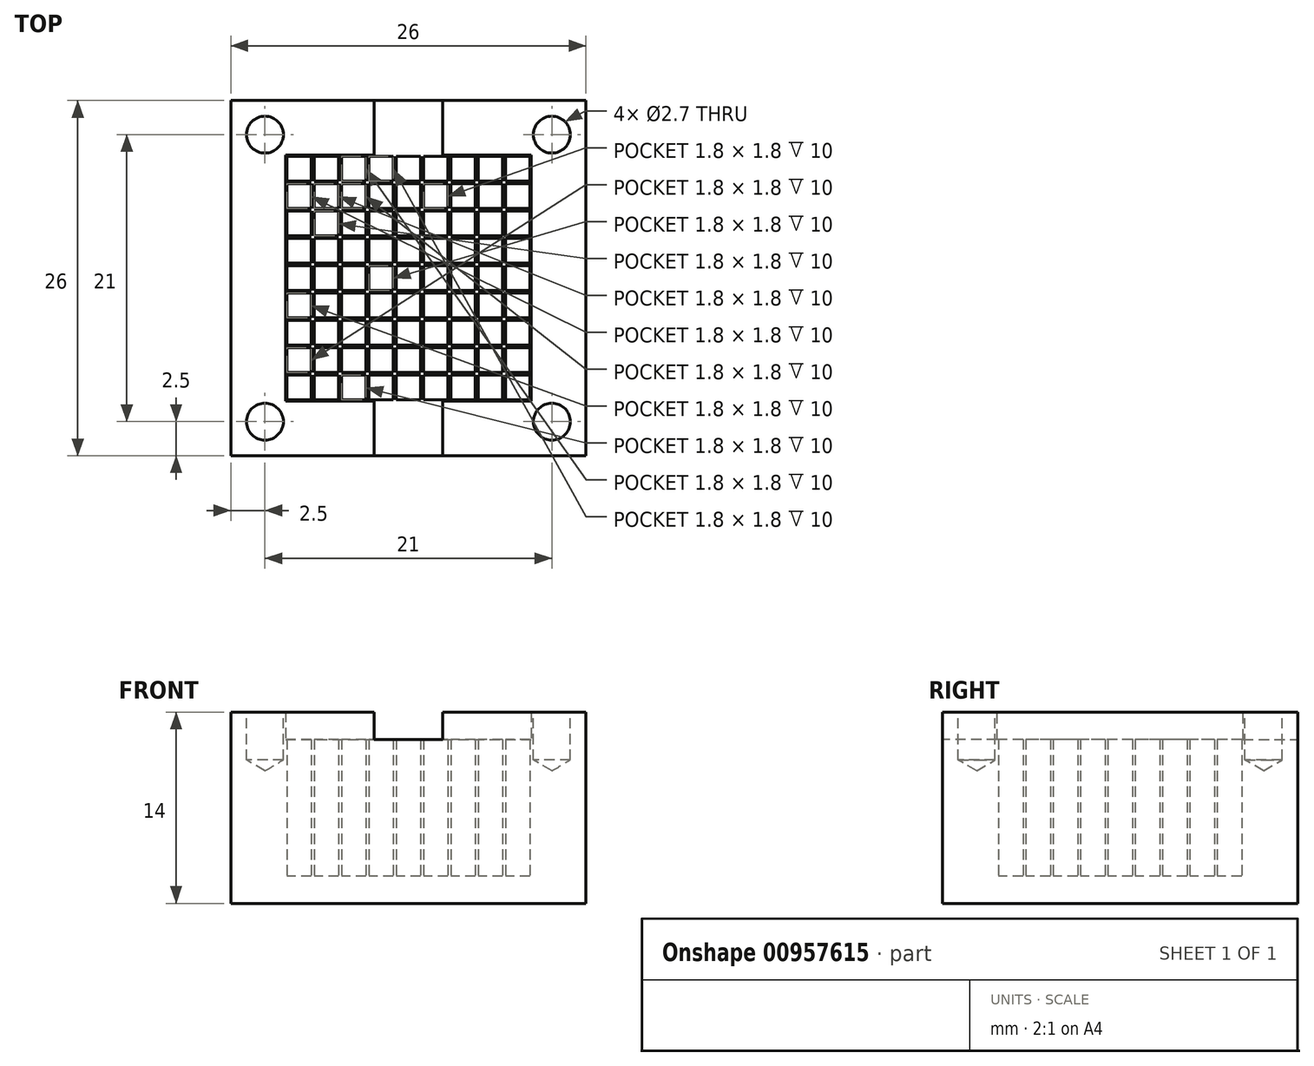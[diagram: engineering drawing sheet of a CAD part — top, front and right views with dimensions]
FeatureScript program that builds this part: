
annotation { "Feature Type Name" : "Feature", "Feature Type Description" : "" }
export const myFeature = defineFeature(function(context is Context, id is Id, definition is map)
    precondition{}
    {
        {
            var Q0;
            Q0=qCreatedBy(makeId("Top.planeOp"),FACE);
            var sketch = newSketch(context, id + "F0", { "sketchPlane" : qUnion([Q0])});
            skLineSegment(sketch, "E0.bottom", {"start": v(-9, 9) * mm, "end": v(9, 9) * mm});
            skLineSegment(sketch, "E0.top", {"start": v(-9, -9) * mm, "end": v(9, -9) * mm});
            skLineSegment(sketch, "E0.left", {"start": v(-9, 9) * mm, "end": v(-9, -9) * mm});
            skLineSegment(sketch, "E0.right", {"start": v(9, 9) * mm, "end": v(9, -9) * mm});
            skPoint(sketch, "E0.middle", {"position": v(0, 0) * mm});
            skLineSegment(sketch, "E1", {"start": v(-8.9, 9) * mm, "end": v(-8.9, -9) * mm});
            skLineSegment(sketch, "E2", {"start": v(-7.1, 9) * mm, "end": v(-7.1, -9) * mm});
            skLineSegment(sketch, "E3", {"start": v(-6.9, 9) * mm, "end": v(-6.9, -9) * mm});
            skLineSegment(sketch, "E4", {"start": v(-5.1, 9) * mm, "end": v(-5.1, -9) * mm});
            skLineSegment(sketch, "E5", {"start": v(-4.9, 9) * mm, "end": v(-4.9, -9) * mm});
            skLineSegment(sketch, "E6", {"start": v(-3.1, 9) * mm, "end": v(-3.1, -9) * mm});
            skLineSegment(sketch, "E7", {"start": v(-2.9, 9) * mm, "end": v(-2.9, -9) * mm});
            skLineSegment(sketch, "E8", {"start": v(-1.1, 9) * mm, "end": v(-1.1, -9) * mm});
            skLineSegment(sketch, "E9", {"start": v(-0.9, 9) * mm, "end": v(-0.9, -9) * mm});
            skLineSegment(sketch, "E10", {"start": v(0.9, 9) * mm, "end": v(0.9, -9) * mm});
            skLineSegment(sketch, "E11", {"start": v(1.1, 9) * mm, "end": v(1.1, -9) * mm});
            skLineSegment(sketch, "E12", {"start": v(2.9, 9) * mm, "end": v(2.9, -9) * mm});
            skLineSegment(sketch, "E13", {"start": v(3.1, 9) * mm, "end": v(3.1, -9) * mm});
            skLineSegment(sketch, "E14", {"start": v(4.9, 9) * mm, "end": v(4.9, -9) * mm});
            skLineSegment(sketch, "E15", {"start": v(5.1, 9) * mm, "end": v(5.1, -9) * mm});
            skLineSegment(sketch, "E16", {"start": v(6.9, 9) * mm, "end": v(6.9, -9) * mm});
            skLineSegment(sketch, "E17", {"start": v(7.1, 9) * mm, "end": v(7.1, -9) * mm});
            skLineSegment(sketch, "E18", {"start": v(8.9, 9) * mm, "end": v(8.9, -9) * mm});
            skLineSegment(sketch, "E19", {"start": v(9, 8.9) * mm, "end": v(-9, 8.9) * mm});
            skLineSegment(sketch, "E20", {"start": v(9, 7.1) * mm, "end": v(-9, 7.1) * mm});
            skLineSegment(sketch, "E21", {"start": v(9, 6.9) * mm, "end": v(-9, 6.9) * mm});
            skLineSegment(sketch, "E22", {"start": v(9, 5.1) * mm, "end": v(-9, 5.1) * mm});
            skLineSegment(sketch, "E23", {"start": v(9, 4.9) * mm, "end": v(-9, 4.9) * mm});
            skLineSegment(sketch, "E24", {"start": v(9, 3.1) * mm, "end": v(-9, 3.1) * mm});
            skLineSegment(sketch, "E25", {"start": v(9, 2.9) * mm, "end": v(-9, 2.9) * mm});
            skLineSegment(sketch, "E26", {"start": v(9, 1.1) * mm, "end": v(-9, 1.1) * mm});
            skLineSegment(sketch, "E27", {"start": v(9, 0.9) * mm, "end": v(-9, 0.9) * mm});
            skLineSegment(sketch, "E28", {"start": v(9, -0.9) * mm, "end": v(-9, -0.9) * mm});
            skLineSegment(sketch, "E29", {"start": v(9, -1.1) * mm, "end": v(-9, -1.1) * mm});
            skLineSegment(sketch, "E30", {"start": v(9, -2.9) * mm, "end": v(-9, -2.9) * mm});
            skLineSegment(sketch, "E31", {"start": v(9, -3.1) * mm, "end": v(-9, -3.1) * mm});
            skLineSegment(sketch, "E32", {"start": v(9, -4.9) * mm, "end": v(-9, -4.9) * mm});
            skLineSegment(sketch, "E33", {"start": v(9, -5.1) * mm, "end": v(-9, -5.1) * mm});
            skLineSegment(sketch, "E34", {"start": v(9, -6.9) * mm, "end": v(-9, -6.9) * mm});
            skLineSegment(sketch, "E35", {"start": v(9, -7.1) * mm, "end": v(-9, -7.1) * mm});
            skLineSegment(sketch, "E36", {"start": v(9, -8.9) * mm, "end": v(-9, -8.9) * mm});
            skSolve(sketch);
        }
        {
            var Q0;
            {var subQ0=sQuery(id+"F0.wireOp",EDGE,"E30");var subQ1=sQuery(id+"F0.wireOp",EDGE,"E10");var subQ2=makeQuery(id+"F0.imprint","INTERSECT",VERTEX,{"derivedFrom":[subQ1,subQ0]});Q0=makeQuery(id+"F0.imprint","IMPRINT",FACE,{"disambiguationData":[TD([[makeQuery(id+"F0.imprint","IMPRINT",EDGE,{"disambiguationData":[TD([[subQ2,-1.0]])],"derivedFrom":subQ1}),1.0]])]});}
            var Q1;
            {var subQ0=sQuery(id+"F0.wireOp",EDGE,"E26");var subQ1=sQuery(id+"F0.wireOp",EDGE,"E11");var subQ2=makeQuery(id+"F0.imprint","INTERSECT",VERTEX,{"derivedFrom":[subQ1,subQ0]});Q1=makeQuery(id+"F0.imprint","IMPRINT",FACE,{"disambiguationData":[TD([[makeQuery(id+"F0.imprint","IMPRINT",EDGE,{"disambiguationData":[TD([[subQ2,-1.0]])],"derivedFrom":subQ1}),1.0]])]});}
            var Q2;
            {var subQ0=sQuery(id+"F0.wireOp",EDGE,"E25");var subQ1=sQuery(id+"F0.wireOp",EDGE,"E8");var subQ2=makeQuery(id+"F0.imprint","INTERSECT",VERTEX,{"derivedFrom":[subQ1,subQ0]});Q2=makeQuery(id+"F0.imprint","IMPRINT",FACE,{"disambiguationData":[TD([[makeQuery(id+"F0.imprint","IMPRINT",EDGE,{"disambiguationData":[TD([[subQ2,-1.0]])],"derivedFrom":subQ1}),1.0]])]});}
            var Q3;
            {var subQ0=sQuery(id+"F0.wireOp",EDGE,"E24");var subQ1=sQuery(id+"F0.wireOp",EDGE,"E10");var subQ2=makeQuery(id+"F0.imprint","INTERSECT",VERTEX,{"derivedFrom":[subQ1,subQ0]});Q3=makeQuery(id+"F0.imprint","IMPRINT",FACE,{"disambiguationData":[TD([[makeQuery(id+"F0.imprint","IMPRINT",EDGE,{"disambiguationData":[TD([[subQ2,-1.0]])],"derivedFrom":subQ1}),1.0]])]});}
            var Q4;
            {var subQ0=sQuery(id+"F0.wireOp",EDGE,"E30");var subQ1=sQuery(id+"F0.wireOp",EDGE,"E15");var subQ2=makeQuery(id+"F0.imprint","INTERSECT",VERTEX,{"derivedFrom":[subQ1,subQ0]});Q4=makeQuery(id+"F0.imprint","IMPRINT",FACE,{"disambiguationData":[TD([[makeQuery(id+"F0.imprint","IMPRINT",EDGE,{"disambiguationData":[TD([[subQ2,-1.0]])],"derivedFrom":subQ1}),1.0]])]});}
            var Q5;
            {var subQ0=sQuery(id+"F0.wireOp",EDGE,"E35");var subQ1=sQuery(id+"F0.wireOp",EDGE,"E12");var subQ2=makeQuery(id+"F0.imprint","INTERSECT",VERTEX,{"derivedFrom":[subQ1,subQ0]});Q5=makeQuery(id+"F0.imprint","IMPRINT",FACE,{"disambiguationData":[TD([[makeQuery(id+"F0.imprint","IMPRINT",EDGE,{"disambiguationData":[TD([[subQ2,-1.0]])],"derivedFrom":subQ1}),1.0]])]});}
            var Q6;
            {var subQ0=sQuery(id+"F0.wireOp",EDGE,"E35");var subQ1=sQuery(id+"F0.wireOp",EDGE,"E14");var subQ2=makeQuery(id+"F0.imprint","INTERSECT",VERTEX,{"derivedFrom":[subQ1,subQ0]});Q6=makeQuery(id+"F0.imprint","IMPRINT",FACE,{"disambiguationData":[TD([[makeQuery(id+"F0.imprint","IMPRINT",EDGE,{"disambiguationData":[TD([[subQ2,-1.0]])],"derivedFrom":subQ1}),1.0]])]});}
            var Q7;
            {var subQ0=sQuery(id+"F0.wireOp",EDGE,"E32");var subQ1=sQuery(id+"F0.wireOp",EDGE,"E10");var subQ2=makeQuery(id+"F0.imprint","INTERSECT",VERTEX,{"derivedFrom":[subQ1,subQ0]});Q7=makeQuery(id+"F0.imprint","IMPRINT",FACE,{"disambiguationData":[TD([[makeQuery(id+"F0.imprint","IMPRINT",EDGE,{"disambiguationData":[TD([[subQ2,-1.0]])],"derivedFrom":subQ1}),1.0]])]});}
            var Q8;
            {var subQ0=sQuery(id+"F0.wireOp",EDGE,"E23");var subQ1=sQuery(id+"F0.wireOp",EDGE,"E14");var subQ2=makeQuery(id+"F0.imprint","INTERSECT",VERTEX,{"derivedFrom":[subQ1,subQ0]});Q8=makeQuery(id+"F0.imprint","IMPRINT",FACE,{"disambiguationData":[TD([[makeQuery(id+"F0.imprint","IMPRINT",EDGE,{"disambiguationData":[TD([[subQ2,-1.0]])],"derivedFrom":subQ1}),1.0]])]});}
            var Q9;
            {var subQ0=sQuery(id+"F0.wireOp",EDGE,"E23");var subQ1=sQuery(id+"F0.wireOp",EDGE,"E16");var subQ2=makeQuery(id+"F0.imprint","INTERSECT",VERTEX,{"derivedFrom":[subQ1,subQ0]});Q9=makeQuery(id+"F0.imprint","IMPRINT",FACE,{"disambiguationData":[TD([[makeQuery(id+"F0.imprint","IMPRINT",EDGE,{"disambiguationData":[TD([[subQ2,-1.0]])],"derivedFrom":subQ1}),1.0]])]});}
            var Q10;
            {var subQ0=sQuery(id+"F0.wireOp",EDGE,"E22");var subQ1=sQuery(id+"F0.wireOp",EDGE,"E9");var subQ2=makeQuery(id+"F0.imprint","INTERSECT",VERTEX,{"derivedFrom":[subQ1,subQ0]});Q10=makeQuery(id+"F0.imprint","IMPRINT",FACE,{"disambiguationData":[TD([[makeQuery(id+"F0.imprint","IMPRINT",EDGE,{"disambiguationData":[TD([[subQ2,-1.0]])],"derivedFrom":subQ1}),1.0]])]});}
            var Q11;
            {var subQ0=sQuery(id+"F0.wireOp",EDGE,"E27");var subQ1=sQuery(id+"F0.wireOp",EDGE,"E10");var subQ2=makeQuery(id+"F0.imprint","INTERSECT",VERTEX,{"derivedFrom":[subQ1,subQ0]});Q11=makeQuery(id+"F0.imprint","IMPRINT",FACE,{"disambiguationData":[TD([[makeQuery(id+"F0.imprint","IMPRINT",EDGE,{"disambiguationData":[TD([[subQ2,-1.0]])],"derivedFrom":subQ1}),1.0]])]});}
            var Q12;
            {var subQ0=sQuery(id+"F0.wireOp",EDGE,"E31");var subQ1=sQuery(id+"F0.wireOp",EDGE,"E2");var subQ2=makeQuery(id+"F0.imprint","INTERSECT",VERTEX,{"derivedFrom":[subQ1,subQ0]});Q12=makeQuery(id+"F0.imprint","IMPRINT",FACE,{"disambiguationData":[TD([[makeQuery(id+"F0.imprint","IMPRINT",EDGE,{"disambiguationData":[TD([[subQ2,-1.0]])],"derivedFrom":subQ1}),1.0]])]});}
            var Q13;
            {var subQ0=sQuery(id+"F0.wireOp",EDGE,"E30");var subQ1=sQuery(id+"F0.wireOp",EDGE,"E13");var subQ2=makeQuery(id+"F0.imprint","INTERSECT",VERTEX,{"derivedFrom":[subQ1,subQ0]});Q13=makeQuery(id+"F0.imprint","IMPRINT",FACE,{"disambiguationData":[TD([[makeQuery(id+"F0.imprint","IMPRINT",EDGE,{"disambiguationData":[TD([[subQ2,-1.0]])],"derivedFrom":subQ1}),1.0]])]});}
            var Q14;
            {var subQ0=sQuery(id+"F0.wireOp",EDGE,"E33");var subQ1=sQuery(id+"F0.wireOp",EDGE,"E16");var subQ2=makeQuery(id+"F0.imprint","INTERSECT",VERTEX,{"derivedFrom":[subQ1,subQ0]});Q14=makeQuery(id+"F0.imprint","IMPRINT",FACE,{"disambiguationData":[TD([[makeQuery(id+"F0.imprint","IMPRINT",EDGE,{"disambiguationData":[TD([[subQ2,-1.0]])],"derivedFrom":subQ1}),1.0]])]});}
            var Q15;
            {var subQ0=sQuery(id+"F0.wireOp",EDGE,"E29");var subQ1=sQuery(id+"F0.wireOp",EDGE,"E8");var subQ2=makeQuery(id+"F0.imprint","INTERSECT",VERTEX,{"derivedFrom":[subQ1,subQ0]});Q15=makeQuery(id+"F0.imprint","IMPRINT",FACE,{"disambiguationData":[TD([[makeQuery(id+"F0.imprint","IMPRINT",EDGE,{"disambiguationData":[TD([[subQ2,-1.0]])],"derivedFrom":subQ1}),1.0]])]});}
            var Q16;
            {var subQ0=sQuery(id+"F0.wireOp",EDGE,"E26");var subQ1=sQuery(id+"F0.wireOp",EDGE,"E1");var subQ2=makeQuery(id+"F0.imprint","INTERSECT",VERTEX,{"derivedFrom":[subQ1,subQ0]});Q16=makeQuery(id+"F0.imprint","IMPRINT",FACE,{"disambiguationData":[TD([[makeQuery(id+"F0.imprint","IMPRINT",EDGE,{"disambiguationData":[TD([[subQ2,-1.0]])],"derivedFrom":subQ1}),1.0]])]});}
            var Q17;
            {var subQ0=sQuery(id+"F0.wireOp",EDGE,"E30");var subQ1=sQuery(id+"F0.wireOp",EDGE,"E12");var subQ2=makeQuery(id+"F0.imprint","INTERSECT",VERTEX,{"derivedFrom":[subQ1,subQ0]});Q17=makeQuery(id+"F0.imprint","IMPRINT",FACE,{"disambiguationData":[TD([[makeQuery(id+"F0.imprint","IMPRINT",EDGE,{"disambiguationData":[TD([[subQ2,-1.0]])],"derivedFrom":subQ1}),1.0]])]});}
            var Q18;
            {var subQ0=sQuery(id+"F0.wireOp",EDGE,"E29");var subQ1=sQuery(id+"F0.wireOp",EDGE,"E12");var subQ2=makeQuery(id+"F0.imprint","INTERSECT",VERTEX,{"derivedFrom":[subQ1,subQ0]});Q18=makeQuery(id+"F0.imprint","IMPRINT",FACE,{"disambiguationData":[TD([[makeQuery(id+"F0.imprint","IMPRINT",EDGE,{"disambiguationData":[TD([[subQ2,-1.0]])],"derivedFrom":subQ1}),1.0]])]});}
            var Q19;
            {var subQ0=sQuery(id+"F0.wireOp",EDGE,"E31");var subQ1=sQuery(id+"F0.wireOp",EDGE,"E6");var subQ2=makeQuery(id+"F0.imprint","INTERSECT",VERTEX,{"derivedFrom":[subQ1,subQ0]});Q19=makeQuery(id+"F0.imprint","IMPRINT",FACE,{"disambiguationData":[TD([[makeQuery(id+"F0.imprint","IMPRINT",EDGE,{"disambiguationData":[TD([[subQ2,-1.0]])],"derivedFrom":subQ1}),1.0]])]});}
            var Q20;
            {var subQ0=sQuery(id+"F0.wireOp",EDGE,"E29");var subQ1=sQuery(id+"F0.wireOp",EDGE,"E10");var subQ2=makeQuery(id+"F0.imprint","INTERSECT",VERTEX,{"derivedFrom":[subQ1,subQ0]});Q20=makeQuery(id+"F0.imprint","IMPRINT",FACE,{"disambiguationData":[TD([[makeQuery(id+"F0.imprint","IMPRINT",EDGE,{"disambiguationData":[TD([[subQ2,-1.0]])],"derivedFrom":subQ1}),1.0]])]});}
            var Q21;
            {var subQ0=sQuery(id+"F0.wireOp",EDGE,"E25");var subQ1=sQuery(id+"F0.wireOp",EDGE,"E16");var subQ2=makeQuery(id+"F0.imprint","INTERSECT",VERTEX,{"derivedFrom":[subQ1,subQ0]});Q21=makeQuery(id+"F0.imprint","IMPRINT",FACE,{"disambiguationData":[TD([[makeQuery(id+"F0.imprint","IMPRINT",EDGE,{"disambiguationData":[TD([[subQ2,-1.0]])],"derivedFrom":subQ1}),1.0]])]});}
            var Q22;
            {var subQ0=sQuery(id+"F0.wireOp",EDGE,"E35");var subQ1=sQuery(id+"F0.wireOp",EDGE,"E16");var subQ2=makeQuery(id+"F0.imprint","INTERSECT",VERTEX,{"derivedFrom":[subQ1,subQ0]});Q22=makeQuery(id+"F0.imprint","IMPRINT",FACE,{"disambiguationData":[TD([[makeQuery(id+"F0.imprint","IMPRINT",EDGE,{"disambiguationData":[TD([[subQ2,-1.0]])],"derivedFrom":subQ1}),1.0]])]});}
            var Q23;
            {var subQ0=sQuery(id+"F0.wireOp",EDGE,"E31");var subQ1=sQuery(id+"F0.wireOp",EDGE,"E12");var subQ2=makeQuery(id+"F0.imprint","INTERSECT",VERTEX,{"derivedFrom":[subQ1,subQ0]});Q23=makeQuery(id+"F0.imprint","IMPRINT",FACE,{"disambiguationData":[TD([[makeQuery(id+"F0.imprint","IMPRINT",EDGE,{"disambiguationData":[TD([[subQ2,-1.0]])],"derivedFrom":subQ1}),1.0]])]});}
            var Q24;
            {var subQ0=sQuery(id+"F0.wireOp",EDGE,"E24");var subQ1=sQuery(id+"F0.wireOp",EDGE,"E1");var subQ2=makeQuery(id+"F0.imprint","INTERSECT",VERTEX,{"derivedFrom":[subQ1,subQ0]});Q24=makeQuery(id+"F0.imprint","IMPRINT",FACE,{"disambiguationData":[TD([[makeQuery(id+"F0.imprint","IMPRINT",EDGE,{"disambiguationData":[TD([[subQ2,-1.0]])],"derivedFrom":subQ1}),1.0]])]});}
            var Q25;
            {var subQ0=sQuery(id+"F0.wireOp",EDGE,"E27");var subQ1=sQuery(id+"F0.wireOp",EDGE,"E16");var subQ2=makeQuery(id+"F0.imprint","INTERSECT",VERTEX,{"derivedFrom":[subQ1,subQ0]});Q25=makeQuery(id+"F0.imprint","IMPRINT",FACE,{"disambiguationData":[TD([[makeQuery(id+"F0.imprint","IMPRINT",EDGE,{"disambiguationData":[TD([[subQ2,-1.0]])],"derivedFrom":subQ1}),1.0]])]});}
            var Q26;
            {var subQ0=sQuery(id+"F0.wireOp",EDGE,"E26");var subQ1=sQuery(id+"F0.wireOp",EDGE,"E9");var subQ2=makeQuery(id+"F0.imprint","INTERSECT",VERTEX,{"derivedFrom":[subQ1,subQ0]});Q26=makeQuery(id+"F0.imprint","IMPRINT",FACE,{"disambiguationData":[TD([[makeQuery(id+"F0.imprint","IMPRINT",EDGE,{"disambiguationData":[TD([[subQ2,-1.0]])],"derivedFrom":subQ1}),1.0]])]});}
            var Q27;
            {var subQ0=sQuery(id+"F0.wireOp",EDGE,"E35");var subQ1=sQuery(id+"F0.wireOp",EDGE,"E2");var subQ2=makeQuery(id+"F0.imprint","INTERSECT",VERTEX,{"derivedFrom":[subQ1,subQ0]});Q27=makeQuery(id+"F0.imprint","IMPRINT",FACE,{"disambiguationData":[TD([[makeQuery(id+"F0.imprint","IMPRINT",EDGE,{"disambiguationData":[TD([[subQ2,-1.0]])],"derivedFrom":subQ1}),1.0]])]});}
            var Q28;
            {var subQ0=sQuery(id+"F0.wireOp",EDGE,"E22");var subQ1=sQuery(id+"F0.wireOp",EDGE,"E16");var subQ2=makeQuery(id+"F0.imprint","INTERSECT",VERTEX,{"derivedFrom":[subQ1,subQ0]});Q28=makeQuery(id+"F0.imprint","IMPRINT",FACE,{"disambiguationData":[TD([[makeQuery(id+"F0.imprint","IMPRINT",EDGE,{"disambiguationData":[TD([[subQ2,-1.0]])],"derivedFrom":subQ1}),1.0]])]});}
            var Q29;
            {var subQ0=sQuery(id+"F0.wireOp",EDGE,"E35");var subQ1=sQuery(id+"F0.wireOp",EDGE,"E8");var subQ2=makeQuery(id+"F0.imprint","INTERSECT",VERTEX,{"derivedFrom":[subQ1,subQ0]});Q29=makeQuery(id+"F0.imprint","IMPRINT",FACE,{"disambiguationData":[TD([[makeQuery(id+"F0.imprint","IMPRINT",EDGE,{"disambiguationData":[TD([[subQ2,-1.0]])],"derivedFrom":subQ1}),1.0]])]});}
            var Q30;
            {var subQ0=sQuery(id+"F0.wireOp",EDGE,"E24");var subQ1=sQuery(id+"F0.wireOp",EDGE,"E7");var subQ2=makeQuery(id+"F0.imprint","INTERSECT",VERTEX,{"derivedFrom":[subQ1,subQ0]});Q30=makeQuery(id+"F0.imprint","IMPRINT",FACE,{"disambiguationData":[TD([[makeQuery(id+"F0.imprint","IMPRINT",EDGE,{"disambiguationData":[TD([[subQ2,-1.0]])],"derivedFrom":subQ1}),1.0]])]});}
            var Q31;
            {var subQ0=sQuery(id+"F0.wireOp",EDGE,"E21");var subQ1=sQuery(id+"F0.wireOp",EDGE,"E16");var subQ2=makeQuery(id+"F0.imprint","INTERSECT",VERTEX,{"derivedFrom":[subQ1,subQ0]});Q31=makeQuery(id+"F0.imprint","IMPRINT",FACE,{"disambiguationData":[TD([[makeQuery(id+"F0.imprint","IMPRINT",EDGE,{"disambiguationData":[TD([[subQ2,-1.0]])],"derivedFrom":subQ1}),1.0]])]});}
            var Q32;
            {var subQ0=sQuery(id+"F0.wireOp",EDGE,"E32");var subQ1=sQuery(id+"F0.wireOp",EDGE,"E11");var subQ2=makeQuery(id+"F0.imprint","INTERSECT",VERTEX,{"derivedFrom":[subQ1,subQ0]});Q32=makeQuery(id+"F0.imprint","IMPRINT",FACE,{"disambiguationData":[TD([[makeQuery(id+"F0.imprint","IMPRINT",EDGE,{"disambiguationData":[TD([[subQ2,-1.0]])],"derivedFrom":subQ1}),1.0]])]});}
            var Q33;
            {var subQ0=sQuery(id+"F0.wireOp",EDGE,"E33");var subQ1=sQuery(id+"F0.wireOp",EDGE,"E8");var subQ2=makeQuery(id+"F0.imprint","INTERSECT",VERTEX,{"derivedFrom":[subQ1,subQ0]});Q33=makeQuery(id+"F0.imprint","IMPRINT",FACE,{"disambiguationData":[TD([[makeQuery(id+"F0.imprint","IMPRINT",EDGE,{"disambiguationData":[TD([[subQ2,-1.0]])],"derivedFrom":subQ1}),1.0]])]});}
            var Q34;
            {var subQ0=sQuery(id+"F0.wireOp",EDGE,"E30");var subQ1=sQuery(id+"F0.wireOp",EDGE,"E9");var subQ2=makeQuery(id+"F0.imprint","INTERSECT",VERTEX,{"derivedFrom":[subQ1,subQ0]});Q34=makeQuery(id+"F0.imprint","IMPRINT",FACE,{"disambiguationData":[TD([[makeQuery(id+"F0.imprint","IMPRINT",EDGE,{"disambiguationData":[TD([[subQ2,-1.0]])],"derivedFrom":subQ1}),1.0]])]});}
            var Q35;
            {var subQ0=sQuery(id+"F0.wireOp",EDGE,"E22");var subQ1=sQuery(id+"F0.wireOp",EDGE,"E8");var subQ2=makeQuery(id+"F0.imprint","INTERSECT",VERTEX,{"derivedFrom":[subQ1,subQ0]});Q35=makeQuery(id+"F0.imprint","IMPRINT",FACE,{"disambiguationData":[TD([[makeQuery(id+"F0.imprint","IMPRINT",EDGE,{"disambiguationData":[TD([[subQ2,-1.0]])],"derivedFrom":subQ1}),1.0]])]});}
            var Q36;
            {var subQ0=sQuery(id+"F0.wireOp",EDGE,"E27");var subQ1=sQuery(id+"F0.wireOp",EDGE,"E2");var subQ2=makeQuery(id+"F0.imprint","INTERSECT",VERTEX,{"derivedFrom":[subQ1,subQ0]});Q36=makeQuery(id+"F0.imprint","IMPRINT",FACE,{"disambiguationData":[TD([[makeQuery(id+"F0.imprint","IMPRINT",EDGE,{"disambiguationData":[TD([[subQ2,-1.0]])],"derivedFrom":subQ1}),1.0]])]});}
            var Q37;
            {var subQ0=sQuery(id+"F0.wireOp",EDGE,"E30");var subQ1=sQuery(id+"F0.wireOp",EDGE,"E11");var subQ2=makeQuery(id+"F0.imprint","INTERSECT",VERTEX,{"derivedFrom":[subQ1,subQ0]});Q37=makeQuery(id+"F0.imprint","IMPRINT",FACE,{"disambiguationData":[TD([[makeQuery(id+"F0.imprint","IMPRINT",EDGE,{"disambiguationData":[TD([[subQ2,-1.0]])],"derivedFrom":subQ1}),1.0]])]});}
            var Q38;
            {var subQ0=sQuery(id+"F0.wireOp",EDGE,"E26");var subQ1=sQuery(id+"F0.wireOp",EDGE,"E5");var subQ2=makeQuery(id+"F0.imprint","INTERSECT",VERTEX,{"derivedFrom":[subQ1,subQ0]});Q38=makeQuery(id+"F0.imprint","IMPRINT",FACE,{"disambiguationData":[TD([[makeQuery(id+"F0.imprint","IMPRINT",EDGE,{"disambiguationData":[TD([[subQ2,-1.0]])],"derivedFrom":subQ1}),1.0]])]});}
            var Q39;
            {var subQ0=sQuery(id+"F0.wireOp",EDGE,"E31");var subQ1=sQuery(id+"F0.wireOp",EDGE,"E8");var subQ2=makeQuery(id+"F0.imprint","INTERSECT",VERTEX,{"derivedFrom":[subQ1,subQ0]});Q39=makeQuery(id+"F0.imprint","IMPRINT",FACE,{"disambiguationData":[TD([[makeQuery(id+"F0.imprint","IMPRINT",EDGE,{"disambiguationData":[TD([[subQ2,-1.0]])],"derivedFrom":subQ1}),1.0]])]});}
            var Q40;
            {var subQ0=sQuery(id+"F0.wireOp",EDGE,"E32");var subQ1=sQuery(id+"F0.wireOp",EDGE,"E7");var subQ2=makeQuery(id+"F0.imprint","INTERSECT",VERTEX,{"derivedFrom":[subQ1,subQ0]});Q40=makeQuery(id+"F0.imprint","IMPRINT",FACE,{"disambiguationData":[TD([[makeQuery(id+"F0.imprint","IMPRINT",EDGE,{"disambiguationData":[TD([[subQ2,-1.0]])],"derivedFrom":subQ1}),1.0]])]});}
            var Q41;
            {var subQ0=sQuery(id+"F0.wireOp",EDGE,"E24");var subQ1=sQuery(id+"F0.wireOp",EDGE,"E17");var subQ2=makeQuery(id+"F0.imprint","INTERSECT",VERTEX,{"derivedFrom":[subQ1,subQ0]});Q41=makeQuery(id+"F0.imprint","IMPRINT",FACE,{"disambiguationData":[TD([[makeQuery(id+"F0.imprint","IMPRINT",EDGE,{"disambiguationData":[TD([[subQ2,-1.0]])],"derivedFrom":subQ1}),1.0]])]});}
            var Q42;
            {var subQ0=sQuery(id+"F0.wireOp",EDGE,"E26");var subQ1=sQuery(id+"F0.wireOp",EDGE,"E14");var subQ2=makeQuery(id+"F0.imprint","INTERSECT",VERTEX,{"derivedFrom":[subQ1,subQ0]});Q42=makeQuery(id+"F0.imprint","IMPRINT",FACE,{"disambiguationData":[TD([[makeQuery(id+"F0.imprint","IMPRINT",EDGE,{"disambiguationData":[TD([[subQ2,-1.0]])],"derivedFrom":subQ1}),1.0]])]});}
            var Q43;
            {var subQ0=sQuery(id+"F0.wireOp",EDGE,"E31");var subQ1=sQuery(id+"F0.wireOp",EDGE,"E14");var subQ2=makeQuery(id+"F0.imprint","INTERSECT",VERTEX,{"derivedFrom":[subQ1,subQ0]});Q43=makeQuery(id+"F0.imprint","IMPRINT",FACE,{"disambiguationData":[TD([[makeQuery(id+"F0.imprint","IMPRINT",EDGE,{"disambiguationData":[TD([[subQ2,-1.0]])],"derivedFrom":subQ1}),1.0]])]});}
            var Q44;
            {var subQ0=sQuery(id+"F0.wireOp",EDGE,"E24");var subQ1=sQuery(id+"F0.wireOp",EDGE,"E5");var subQ2=makeQuery(id+"F0.imprint","INTERSECT",VERTEX,{"derivedFrom":[subQ1,subQ0]});Q44=makeQuery(id+"F0.imprint","IMPRINT",FACE,{"disambiguationData":[TD([[makeQuery(id+"F0.imprint","IMPRINT",EDGE,{"disambiguationData":[TD([[subQ2,-1.0]])],"derivedFrom":subQ1}),1.0]])]});}
            var Q45;
            {var subQ0=sQuery(id+"F0.wireOp",EDGE,"E26");var subQ1=sQuery(id+"F0.wireOp",EDGE,"E12");var subQ2=makeQuery(id+"F0.imprint","INTERSECT",VERTEX,{"derivedFrom":[subQ1,subQ0]});Q45=makeQuery(id+"F0.imprint","IMPRINT",FACE,{"disambiguationData":[TD([[makeQuery(id+"F0.imprint","IMPRINT",EDGE,{"disambiguationData":[TD([[subQ2,-1.0]])],"derivedFrom":subQ1}),1.0]])]});}
            var Q46;
            {var subQ0=sQuery(id+"F0.wireOp",EDGE,"E30");var subQ1=sQuery(id+"F0.wireOp",EDGE,"E5");var subQ2=makeQuery(id+"F0.imprint","INTERSECT",VERTEX,{"derivedFrom":[subQ1,subQ0]});Q46=makeQuery(id+"F0.imprint","IMPRINT",FACE,{"disambiguationData":[TD([[makeQuery(id+"F0.imprint","IMPRINT",EDGE,{"disambiguationData":[TD([[subQ2,-1.0]])],"derivedFrom":subQ1}),1.0]])]});}
            var Q47;
            {var subQ0=sQuery(id+"F0.wireOp",EDGE,"E33");var subQ1=sQuery(id+"F0.wireOp",EDGE,"E14");var subQ2=makeQuery(id+"F0.imprint","INTERSECT",VERTEX,{"derivedFrom":[subQ1,subQ0]});Q47=makeQuery(id+"F0.imprint","IMPRINT",FACE,{"disambiguationData":[TD([[makeQuery(id+"F0.imprint","IMPRINT",EDGE,{"disambiguationData":[TD([[subQ2,-1.0]])],"derivedFrom":subQ1}),1.0]])]});}
            var Q48;
            {var subQ0=sQuery(id+"F0.wireOp",EDGE,"E32");var subQ1=sQuery(id+"F0.wireOp",EDGE,"E9");var subQ2=makeQuery(id+"F0.imprint","INTERSECT",VERTEX,{"derivedFrom":[subQ1,subQ0]});Q48=makeQuery(id+"F0.imprint","IMPRINT",FACE,{"disambiguationData":[TD([[makeQuery(id+"F0.imprint","IMPRINT",EDGE,{"disambiguationData":[TD([[subQ2,-1.0]])],"derivedFrom":subQ1}),1.0]])]});}
            var Q49;
            {var subQ0=sQuery(id+"F0.wireOp",EDGE,"E25");var subQ1=sQuery(id+"F0.wireOp",EDGE,"E6");var subQ2=makeQuery(id+"F0.imprint","INTERSECT",VERTEX,{"derivedFrom":[subQ1,subQ0]});Q49=makeQuery(id+"F0.imprint","IMPRINT",FACE,{"disambiguationData":[TD([[makeQuery(id+"F0.imprint","IMPRINT",EDGE,{"disambiguationData":[TD([[subQ2,-1.0]])],"derivedFrom":subQ1}),1.0]])]});}
            var Q50;
            {var subQ0=sQuery(id+"F0.wireOp",EDGE,"E19");var subQ1=sQuery(id+"F0.wireOp",EDGE,"E16");var subQ2=makeQuery(id+"F0.imprint","INTERSECT",VERTEX,{"derivedFrom":[subQ1,subQ0]});Q50=makeQuery(id+"F0.imprint","IMPRINT",FACE,{"disambiguationData":[TD([[makeQuery(id+"F0.imprint","IMPRINT",EDGE,{"disambiguationData":[TD([[subQ2,-1.0]])],"derivedFrom":subQ1}),1.0]])]});}
            var Q51;
            {var subQ0=sQuery(id+"F0.wireOp",EDGE,"E19");var subQ1=sQuery(id+"F0.wireOp",EDGE,"E10");var subQ2=makeQuery(id+"F0.imprint","INTERSECT",VERTEX,{"derivedFrom":[subQ1,subQ0]});Q51=makeQuery(id+"F0.imprint","IMPRINT",FACE,{"disambiguationData":[TD([[makeQuery(id+"F0.imprint","IMPRINT",EDGE,{"disambiguationData":[TD([[subQ2,-1.0]])],"derivedFrom":subQ1}),1.0]])]});}
            var Q52;
            {var subQ0=sQuery(id+"F0.wireOp",EDGE,"E19");var subQ1=sQuery(id+"F0.wireOp",EDGE,"E2");var subQ2=makeQuery(id+"F0.imprint","INTERSECT",VERTEX,{"derivedFrom":[subQ1,subQ0]});Q52=makeQuery(id+"F0.imprint","IMPRINT",FACE,{"disambiguationData":[TD([[makeQuery(id+"F0.imprint","IMPRINT",EDGE,{"disambiguationData":[TD([[subQ2,-1.0]])],"derivedFrom":subQ1}),1.0]])]});}
            var Q53;
            {var subQ0=sQuery(id+"F0.wireOp",EDGE,"E32");var subQ1=sQuery(id+"F0.wireOp",EDGE,"E17");var subQ2=makeQuery(id+"F0.imprint","INTERSECT",VERTEX,{"derivedFrom":[subQ1,subQ0]});Q53=makeQuery(id+"F0.imprint","IMPRINT",FACE,{"disambiguationData":[TD([[makeQuery(id+"F0.imprint","IMPRINT",EDGE,{"disambiguationData":[TD([[subQ2,-1.0]])],"derivedFrom":subQ1}),1.0]])]});}
            var Q54;
            {var subQ0=sQuery(id+"F0.wireOp",EDGE,"E30");var subQ1=sQuery(id+"F0.wireOp",EDGE,"E17");var subQ2=makeQuery(id+"F0.imprint","INTERSECT",VERTEX,{"derivedFrom":[subQ1,subQ0]});Q54=makeQuery(id+"F0.imprint","IMPRINT",FACE,{"disambiguationData":[TD([[makeQuery(id+"F0.imprint","IMPRINT",EDGE,{"disambiguationData":[TD([[subQ2,-1.0]])],"derivedFrom":subQ1}),1.0]])]});}
            var Q55;
            {var subQ0=sQuery(id+"F0.wireOp",EDGE,"E33");var subQ1=sQuery(id+"F0.wireOp",EDGE,"E12");var subQ2=makeQuery(id+"F0.imprint","INTERSECT",VERTEX,{"derivedFrom":[subQ1,subQ0]});Q55=makeQuery(id+"F0.imprint","IMPRINT",FACE,{"disambiguationData":[TD([[makeQuery(id+"F0.imprint","IMPRINT",EDGE,{"disambiguationData":[TD([[subQ2,-1.0]])],"derivedFrom":subQ1}),1.0]])]});}
            var Q56;
            {var subQ0=sQuery(id+"F0.wireOp",EDGE,"E24");var subQ1=sQuery(id+"F0.wireOp",EDGE,"E8");var subQ2=makeQuery(id+"F0.imprint","INTERSECT",VERTEX,{"derivedFrom":[subQ1,subQ0]});Q56=makeQuery(id+"F0.imprint","IMPRINT",FACE,{"disambiguationData":[TD([[makeQuery(id+"F0.imprint","IMPRINT",EDGE,{"disambiguationData":[TD([[subQ2,-1.0]])],"derivedFrom":subQ1}),1.0]])]});}
            var Q57;
            {var subQ0=sQuery(id+"F0.wireOp",EDGE,"E22");var subQ1=sQuery(id+"F0.wireOp",EDGE,"E13");var subQ2=makeQuery(id+"F0.imprint","INTERSECT",VERTEX,{"derivedFrom":[subQ1,subQ0]});Q57=makeQuery(id+"F0.imprint","IMPRINT",FACE,{"disambiguationData":[TD([[makeQuery(id+"F0.imprint","IMPRINT",EDGE,{"disambiguationData":[TD([[subQ2,-1.0]])],"derivedFrom":subQ1}),1.0]])]});}
            var Q58;
            {var subQ0=sQuery(id+"F0.wireOp",EDGE,"E19");var subQ1=sQuery(id+"F0.wireOp",EDGE,"E14");var subQ2=makeQuery(id+"F0.imprint","INTERSECT",VERTEX,{"derivedFrom":[subQ1,subQ0]});Q58=makeQuery(id+"F0.imprint","IMPRINT",FACE,{"disambiguationData":[TD([[makeQuery(id+"F0.imprint","IMPRINT",EDGE,{"disambiguationData":[TD([[subQ2,-1.0]])],"derivedFrom":subQ1}),1.0]])]});}
            var Q59;
            {var subQ0=sQuery(id+"F0.wireOp",EDGE,"E26");var subQ1=sQuery(id+"F0.wireOp",EDGE,"E3");var subQ2=makeQuery(id+"F0.imprint","INTERSECT",VERTEX,{"derivedFrom":[subQ1,subQ0]});Q59=makeQuery(id+"F0.imprint","IMPRINT",FACE,{"disambiguationData":[TD([[makeQuery(id+"F0.imprint","IMPRINT",EDGE,{"disambiguationData":[TD([[subQ2,-1.0]])],"derivedFrom":subQ1}),1.0]])]});}
            var Q60;
            {var subQ0=sQuery(id+"F0.wireOp",EDGE,"E32");var subQ1=sQuery(id+"F0.wireOp",EDGE,"E16");var subQ2=makeQuery(id+"F0.imprint","INTERSECT",VERTEX,{"derivedFrom":[subQ1,subQ0]});Q60=makeQuery(id+"F0.imprint","IMPRINT",FACE,{"disambiguationData":[TD([[makeQuery(id+"F0.imprint","IMPRINT",EDGE,{"disambiguationData":[TD([[subQ2,-1.0]])],"derivedFrom":subQ1}),1.0]])]});}
            var Q61;
            {var subQ0=sQuery(id+"F0.wireOp",EDGE,"E32");var subQ1=sQuery(id+"F0.wireOp",EDGE,"E3");var subQ2=makeQuery(id+"F0.imprint","INTERSECT",VERTEX,{"derivedFrom":[subQ1,subQ0]});Q61=makeQuery(id+"F0.imprint","IMPRINT",FACE,{"disambiguationData":[TD([[makeQuery(id+"F0.imprint","IMPRINT",EDGE,{"disambiguationData":[TD([[subQ2,-1.0]])],"derivedFrom":subQ1}),1.0]])]});}
            var Q62;
            {var subQ0=sQuery(id+"F0.wireOp",EDGE,"E32");var subQ1=sQuery(id+"F0.wireOp",EDGE,"E6");var subQ2=makeQuery(id+"F0.imprint","INTERSECT",VERTEX,{"derivedFrom":[subQ1,subQ0]});Q62=makeQuery(id+"F0.imprint","IMPRINT",FACE,{"disambiguationData":[TD([[makeQuery(id+"F0.imprint","IMPRINT",EDGE,{"disambiguationData":[TD([[subQ2,-1.0]])],"derivedFrom":subQ1}),1.0]])]});}
            var Q63;
            {var subQ0=sQuery(id+"F0.wireOp",EDGE,"E35");var subQ1=sQuery(id+"F0.wireOp",EDGE,"E10");var subQ2=makeQuery(id+"F0.imprint","INTERSECT",VERTEX,{"derivedFrom":[subQ1,subQ0]});Q63=makeQuery(id+"F0.imprint","IMPRINT",FACE,{"disambiguationData":[TD([[makeQuery(id+"F0.imprint","IMPRINT",EDGE,{"disambiguationData":[TD([[subQ2,-1.0]])],"derivedFrom":subQ1}),1.0]])]});}
            var Q64;
            {var subQ0=sQuery(id+"F0.wireOp",EDGE,"E23");var subQ1=sQuery(id+"F0.wireOp",EDGE,"E12");var subQ2=makeQuery(id+"F0.imprint","INTERSECT",VERTEX,{"derivedFrom":[subQ1,subQ0]});Q64=makeQuery(id+"F0.imprint","IMPRINT",FACE,{"disambiguationData":[TD([[makeQuery(id+"F0.imprint","IMPRINT",EDGE,{"disambiguationData":[TD([[subQ2,-1.0]])],"derivedFrom":subQ1}),1.0]])]});}
            var Q65;
            {var subQ0=sQuery(id+"F0.wireOp",EDGE,"E32");var subQ1=sQuery(id+"F0.wireOp",EDGE,"E5");var subQ2=makeQuery(id+"F0.imprint","INTERSECT",VERTEX,{"derivedFrom":[subQ1,subQ0]});Q65=makeQuery(id+"F0.imprint","IMPRINT",FACE,{"disambiguationData":[TD([[makeQuery(id+"F0.imprint","IMPRINT",EDGE,{"disambiguationData":[TD([[subQ2,-1.0]])],"derivedFrom":subQ1}),1.0]])]});}
            var Q66;
            {var subQ0=sQuery(id+"F0.wireOp",EDGE,"E33");var subQ1=sQuery(id+"F0.wireOp",EDGE,"E6");var subQ2=makeQuery(id+"F0.imprint","INTERSECT",VERTEX,{"derivedFrom":[subQ1,subQ0]});Q66=makeQuery(id+"F0.imprint","IMPRINT",FACE,{"disambiguationData":[TD([[makeQuery(id+"F0.imprint","IMPRINT",EDGE,{"disambiguationData":[TD([[subQ2,-1.0]])],"derivedFrom":subQ1}),1.0]])]});}
            var Q67;
            {var subQ0=sQuery(id+"F0.wireOp",EDGE,"E30");var subQ1=sQuery(id+"F0.wireOp",EDGE,"E7");var subQ2=makeQuery(id+"F0.imprint","INTERSECT",VERTEX,{"derivedFrom":[subQ1,subQ0]});Q67=makeQuery(id+"F0.imprint","IMPRINT",FACE,{"disambiguationData":[TD([[makeQuery(id+"F0.imprint","IMPRINT",EDGE,{"disambiguationData":[TD([[subQ2,-1.0]])],"derivedFrom":subQ1}),1.0]])]});}
            var Q68;
            {var subQ0=sQuery(id+"F0.wireOp",EDGE,"E33");var subQ1=sQuery(id+"F0.wireOp",EDGE,"E10");var subQ2=makeQuery(id+"F0.imprint","INTERSECT",VERTEX,{"derivedFrom":[subQ1,subQ0]});Q68=makeQuery(id+"F0.imprint","IMPRINT",FACE,{"disambiguationData":[TD([[makeQuery(id+"F0.imprint","IMPRINT",EDGE,{"disambiguationData":[TD([[subQ2,-1.0]])],"derivedFrom":subQ1}),1.0]])]});}
            var Q69;
            {var subQ0=sQuery(id+"F0.wireOp",EDGE,"E30");var subQ1=sQuery(id+"F0.wireOp",EDGE,"E14");var subQ2=makeQuery(id+"F0.imprint","INTERSECT",VERTEX,{"derivedFrom":[subQ1,subQ0]});Q69=makeQuery(id+"F0.imprint","IMPRINT",FACE,{"disambiguationData":[TD([[makeQuery(id+"F0.imprint","IMPRINT",EDGE,{"disambiguationData":[TD([[subQ2,-1.0]])],"derivedFrom":subQ1}),1.0]])]});}
            var Q70;
            {var subQ0=sQuery(id+"F0.wireOp",EDGE,"E26");var subQ1=sQuery(id+"F0.wireOp",EDGE,"E13");var subQ2=makeQuery(id+"F0.imprint","INTERSECT",VERTEX,{"derivedFrom":[subQ1,subQ0]});Q70=makeQuery(id+"F0.imprint","IMPRINT",FACE,{"disambiguationData":[TD([[makeQuery(id+"F0.imprint","IMPRINT",EDGE,{"disambiguationData":[TD([[subQ2,-1.0]])],"derivedFrom":subQ1}),1.0]])]});}
            var Q71;
            {var subQ0=sQuery(id+"F0.wireOp",EDGE,"E26");var subQ1=sQuery(id+"F0.wireOp",EDGE,"E16");var subQ2=makeQuery(id+"F0.imprint","INTERSECT",VERTEX,{"derivedFrom":[subQ1,subQ0]});Q71=makeQuery(id+"F0.imprint","IMPRINT",FACE,{"disambiguationData":[TD([[makeQuery(id+"F0.imprint","IMPRINT",EDGE,{"disambiguationData":[TD([[subQ2,-1.0]])],"derivedFrom":subQ1}),1.0]])]});}
            var Q72;
            {var subQ0=sQuery(id+"F0.wireOp",EDGE,"E32");var subQ1=sQuery(id+"F0.wireOp",EDGE,"E14");var subQ2=makeQuery(id+"F0.imprint","INTERSECT",VERTEX,{"derivedFrom":[subQ1,subQ0]});Q72=makeQuery(id+"F0.imprint","IMPRINT",FACE,{"disambiguationData":[TD([[makeQuery(id+"F0.imprint","IMPRINT",EDGE,{"disambiguationData":[TD([[subQ2,-1.0]])],"derivedFrom":subQ1}),1.0]])]});}
            var Q73;
            {var subQ0=sQuery(id+"F0.wireOp",EDGE,"E24");var subQ1=sQuery(id+"F0.wireOp",EDGE,"E11");var subQ2=makeQuery(id+"F0.imprint","INTERSECT",VERTEX,{"derivedFrom":[subQ1,subQ0]});Q73=makeQuery(id+"F0.imprint","IMPRINT",FACE,{"disambiguationData":[TD([[makeQuery(id+"F0.imprint","IMPRINT",EDGE,{"disambiguationData":[TD([[subQ2,-1.0]])],"derivedFrom":subQ1}),1.0]])]});}
            var Q74;
            {var subQ0=sQuery(id+"F0.wireOp",EDGE,"E30");var subQ1=sQuery(id+"F0.wireOp",EDGE,"E3");var subQ2=makeQuery(id+"F0.imprint","INTERSECT",VERTEX,{"derivedFrom":[subQ1,subQ0]});Q74=makeQuery(id+"F0.imprint","IMPRINT",FACE,{"disambiguationData":[TD([[makeQuery(id+"F0.imprint","IMPRINT",EDGE,{"disambiguationData":[TD([[subQ2,-1.0]])],"derivedFrom":subQ1}),1.0]])]});}
            var Q75;
            {var subQ0=sQuery(id+"F0.wireOp",EDGE,"E22");var subQ1=sQuery(id+"F0.wireOp",EDGE,"E14");var subQ2=makeQuery(id+"F0.imprint","INTERSECT",VERTEX,{"derivedFrom":[subQ1,subQ0]});Q75=makeQuery(id+"F0.imprint","IMPRINT",FACE,{"disambiguationData":[TD([[makeQuery(id+"F0.imprint","IMPRINT",EDGE,{"disambiguationData":[TD([[subQ2,-1.0]])],"derivedFrom":subQ1}),1.0]])]});}
            var Q76;
            {var subQ0=sQuery(id+"F0.wireOp",EDGE,"E22");var subQ1=sQuery(id+"F0.wireOp",EDGE,"E15");var subQ2=makeQuery(id+"F0.imprint","INTERSECT",VERTEX,{"derivedFrom":[subQ1,subQ0]});Q76=makeQuery(id+"F0.imprint","IMPRINT",FACE,{"disambiguationData":[TD([[makeQuery(id+"F0.imprint","IMPRINT",EDGE,{"disambiguationData":[TD([[subQ2,-1.0]])],"derivedFrom":subQ1}),1.0]])]});}
            var Q77;
            {var subQ0=sQuery(id+"F0.wireOp",EDGE,"E29");var subQ1=sQuery(id+"F0.wireOp",EDGE,"E16");var subQ2=makeQuery(id+"F0.imprint","INTERSECT",VERTEX,{"derivedFrom":[subQ1,subQ0]});Q77=makeQuery(id+"F0.imprint","IMPRINT",FACE,{"disambiguationData":[TD([[makeQuery(id+"F0.imprint","IMPRINT",EDGE,{"disambiguationData":[TD([[subQ2,-1.0]])],"derivedFrom":subQ1}),1.0]])]});}
            var Q78;
            {var subQ0=sQuery(id+"F0.wireOp",EDGE,"E22");var subQ1=sQuery(id+"F0.wireOp",EDGE,"E17");var subQ2=makeQuery(id+"F0.imprint","INTERSECT",VERTEX,{"derivedFrom":[subQ1,subQ0]});Q78=makeQuery(id+"F0.imprint","IMPRINT",FACE,{"disambiguationData":[TD([[makeQuery(id+"F0.imprint","IMPRINT",EDGE,{"disambiguationData":[TD([[subQ2,-1.0]])],"derivedFrom":subQ1}),1.0]])]});}
            var Q79;
            {var subQ0=sQuery(id+"F0.wireOp",EDGE,"E30");var subQ1=sQuery(id+"F0.wireOp",EDGE,"E6");var subQ2=makeQuery(id+"F0.imprint","INTERSECT",VERTEX,{"derivedFrom":[subQ1,subQ0]});Q79=makeQuery(id+"F0.imprint","IMPRINT",FACE,{"disambiguationData":[TD([[makeQuery(id+"F0.imprint","IMPRINT",EDGE,{"disambiguationData":[TD([[subQ2,-1.0]])],"derivedFrom":subQ1}),1.0]])]});}
            var Q80;
            {var subQ0=sQuery(id+"F0.wireOp",EDGE,"E21");var subQ1=sQuery(id+"F0.wireOp",EDGE,"E10");var subQ2=makeQuery(id+"F0.imprint","INTERSECT",VERTEX,{"derivedFrom":[subQ1,subQ0]});Q80=makeQuery(id+"F0.imprint","IMPRINT",FACE,{"disambiguationData":[TD([[makeQuery(id+"F0.imprint","IMPRINT",EDGE,{"disambiguationData":[TD([[subQ2,-1.0]])],"derivedFrom":subQ1}),1.0]])]});}
            var Q81;
            {var subQ0=sQuery(id+"F0.wireOp",EDGE,"E23");var subQ1=sQuery(id+"F0.wireOp",EDGE,"E10");var subQ2=makeQuery(id+"F0.imprint","INTERSECT",VERTEX,{"derivedFrom":[subQ1,subQ0]});Q81=makeQuery(id+"F0.imprint","IMPRINT",FACE,{"disambiguationData":[TD([[makeQuery(id+"F0.imprint","IMPRINT",EDGE,{"disambiguationData":[TD([[subQ2,-1.0]])],"derivedFrom":subQ1}),1.0]])]});}
            var Q82;
            {var subQ0=sQuery(id+"F0.wireOp",EDGE,"E24");var subQ1=sQuery(id+"F0.wireOp",EDGE,"E6");var subQ2=makeQuery(id+"F0.imprint","INTERSECT",VERTEX,{"derivedFrom":[subQ1,subQ0]});Q82=makeQuery(id+"F0.imprint","IMPRINT",FACE,{"disambiguationData":[TD([[makeQuery(id+"F0.imprint","IMPRINT",EDGE,{"disambiguationData":[TD([[subQ2,-1.0]])],"derivedFrom":subQ1}),1.0]])]});}
            var Q83;
            {var subQ0=sQuery(id+"F0.wireOp",EDGE,"E32");var subQ1=sQuery(id+"F0.wireOp",EDGE,"E1");var subQ2=makeQuery(id+"F0.imprint","INTERSECT",VERTEX,{"derivedFrom":[subQ1,subQ0]});Q83=makeQuery(id+"F0.imprint","IMPRINT",FACE,{"disambiguationData":[TD([[makeQuery(id+"F0.imprint","IMPRINT",EDGE,{"disambiguationData":[TD([[subQ2,-1.0]])],"derivedFrom":subQ1}),1.0]])]});}
            var Q84;
            {var subQ0=sQuery(id+"F0.wireOp",EDGE,"E24");var subQ1=sQuery(id+"F0.wireOp",EDGE,"E12");var subQ2=makeQuery(id+"F0.imprint","INTERSECT",VERTEX,{"derivedFrom":[subQ1,subQ0]});Q84=makeQuery(id+"F0.imprint","IMPRINT",FACE,{"disambiguationData":[TD([[makeQuery(id+"F0.imprint","IMPRINT",EDGE,{"disambiguationData":[TD([[subQ2,-1.0]])],"derivedFrom":subQ1}),1.0]])]});}
            var Q85;
            {var subQ0=sQuery(id+"F0.wireOp",EDGE,"E25");var subQ1=sQuery(id+"F0.wireOp",EDGE,"E2");var subQ2=makeQuery(id+"F0.imprint","INTERSECT",VERTEX,{"derivedFrom":[subQ1,subQ0]});Q85=makeQuery(id+"F0.imprint","IMPRINT",FACE,{"disambiguationData":[TD([[makeQuery(id+"F0.imprint","IMPRINT",EDGE,{"disambiguationData":[TD([[subQ2,-1.0]])],"derivedFrom":subQ1}),1.0]])]});}
            var Q86;
            {var subQ0=sQuery(id+"F0.wireOp",EDGE,"E25");var subQ1=sQuery(id+"F0.wireOp",EDGE,"E14");var subQ2=makeQuery(id+"F0.imprint","INTERSECT",VERTEX,{"derivedFrom":[subQ1,subQ0]});Q86=makeQuery(id+"F0.imprint","IMPRINT",FACE,{"disambiguationData":[TD([[makeQuery(id+"F0.imprint","IMPRINT",EDGE,{"disambiguationData":[TD([[subQ2,-1.0]])],"derivedFrom":subQ1}),1.0]])]});}
            var Q87;
            {var subQ0=sQuery(id+"F0.wireOp",EDGE,"E26");var subQ1=sQuery(id+"F0.wireOp",EDGE,"E6");var subQ2=makeQuery(id+"F0.imprint","INTERSECT",VERTEX,{"derivedFrom":[subQ1,subQ0]});Q87=makeQuery(id+"F0.imprint","IMPRINT",FACE,{"disambiguationData":[TD([[makeQuery(id+"F0.imprint","IMPRINT",EDGE,{"disambiguationData":[TD([[subQ2,-1.0]])],"derivedFrom":subQ1}),1.0]])]});}
            var Q88;
            {var subQ0=sQuery(id+"F0.wireOp",EDGE,"E22");var subQ1=sQuery(id+"F0.wireOp",EDGE,"E3");var subQ2=makeQuery(id+"F0.imprint","INTERSECT",VERTEX,{"derivedFrom":[subQ1,subQ0]});Q88=makeQuery(id+"F0.imprint","IMPRINT",FACE,{"disambiguationData":[TD([[makeQuery(id+"F0.imprint","IMPRINT",EDGE,{"disambiguationData":[TD([[subQ2,-1.0]])],"derivedFrom":subQ1}),1.0]])]});}
            var Q89;
            {var subQ0=sQuery(id+"F0.wireOp",EDGE,"E24");var subQ1=sQuery(id+"F0.wireOp",EDGE,"E13");var subQ2=makeQuery(id+"F0.imprint","INTERSECT",VERTEX,{"derivedFrom":[subQ1,subQ0]});Q89=makeQuery(id+"F0.imprint","IMPRINT",FACE,{"disambiguationData":[TD([[makeQuery(id+"F0.imprint","IMPRINT",EDGE,{"disambiguationData":[TD([[subQ2,-1.0]])],"derivedFrom":subQ1}),1.0]])]});}
            var Q90;
            {var subQ0=sQuery(id+"F0.wireOp",EDGE,"E31");var subQ1=sQuery(id+"F0.wireOp",EDGE,"E10");var subQ2=makeQuery(id+"F0.imprint","INTERSECT",VERTEX,{"derivedFrom":[subQ1,subQ0]});Q90=makeQuery(id+"F0.imprint","IMPRINT",FACE,{"disambiguationData":[TD([[makeQuery(id+"F0.imprint","IMPRINT",EDGE,{"disambiguationData":[TD([[subQ2,-1.0]])],"derivedFrom":subQ1}),1.0]])]});}
            var Q91;
            {var subQ0=sQuery(id+"F0.wireOp",EDGE,"E26");var subQ1=sQuery(id+"F0.wireOp",EDGE,"E8");var subQ2=makeQuery(id+"F0.imprint","INTERSECT",VERTEX,{"derivedFrom":[subQ1,subQ0]});Q91=makeQuery(id+"F0.imprint","IMPRINT",FACE,{"disambiguationData":[TD([[makeQuery(id+"F0.imprint","IMPRINT",EDGE,{"disambiguationData":[TD([[subQ2,-1.0]])],"derivedFrom":subQ1}),1.0]])]});}
            var Q92;
            {var subQ0=sQuery(id+"F0.wireOp",EDGE,"E32");var subQ1=sQuery(id+"F0.wireOp",EDGE,"E12");var subQ2=makeQuery(id+"F0.imprint","INTERSECT",VERTEX,{"derivedFrom":[subQ1,subQ0]});Q92=makeQuery(id+"F0.imprint","IMPRINT",FACE,{"disambiguationData":[TD([[makeQuery(id+"F0.imprint","IMPRINT",EDGE,{"disambiguationData":[TD([[subQ2,-1.0]])],"derivedFrom":subQ1}),1.0]])]});}
            var Q93;
            {var subQ0=sQuery(id+"F0.wireOp",EDGE,"E23");var subQ1=sQuery(id+"F0.wireOp",EDGE,"E6");var subQ2=makeQuery(id+"F0.imprint","INTERSECT",VERTEX,{"derivedFrom":[subQ1,subQ0]});Q93=makeQuery(id+"F0.imprint","IMPRINT",FACE,{"disambiguationData":[TD([[makeQuery(id+"F0.imprint","IMPRINT",EDGE,{"disambiguationData":[TD([[subQ2,-1.0]])],"derivedFrom":subQ1}),1.0]])]});}
            var Q94;
            {var subQ0=sQuery(id+"F0.wireOp",EDGE,"E32");var subQ1=sQuery(id+"F0.wireOp",EDGE,"E8");var subQ2=makeQuery(id+"F0.imprint","INTERSECT",VERTEX,{"derivedFrom":[subQ1,subQ0]});Q94=makeQuery(id+"F0.imprint","IMPRINT",FACE,{"disambiguationData":[TD([[makeQuery(id+"F0.imprint","IMPRINT",EDGE,{"disambiguationData":[TD([[subQ2,-1.0]])],"derivedFrom":subQ1}),1.0]])]});}
            var Q95;
            {var subQ0=sQuery(id+"F0.wireOp",EDGE,"E27");var subQ1=sQuery(id+"F0.wireOp",EDGE,"E14");var subQ2=makeQuery(id+"F0.imprint","INTERSECT",VERTEX,{"derivedFrom":[subQ1,subQ0]});Q95=makeQuery(id+"F0.imprint","IMPRINT",FACE,{"disambiguationData":[TD([[makeQuery(id+"F0.imprint","IMPRINT",EDGE,{"disambiguationData":[TD([[subQ2,-1.0]])],"derivedFrom":subQ1}),1.0]])]});}
            var Q96;
            {var subQ0=sQuery(id+"F0.wireOp",EDGE,"E24");var subQ1=sQuery(id+"F0.wireOp",EDGE,"E3");var subQ2=makeQuery(id+"F0.imprint","INTERSECT",VERTEX,{"derivedFrom":[subQ1,subQ0]});Q96=makeQuery(id+"F0.imprint","IMPRINT",FACE,{"disambiguationData":[TD([[makeQuery(id+"F0.imprint","IMPRINT",EDGE,{"disambiguationData":[TD([[subQ2,-1.0]])],"derivedFrom":subQ1}),1.0]])]});}
            var Q97;
            {var subQ0=sQuery(id+"F0.wireOp",EDGE,"E22");var subQ1=sQuery(id+"F0.wireOp",EDGE,"E1");var subQ2=makeQuery(id+"F0.imprint","INTERSECT",VERTEX,{"derivedFrom":[subQ1,subQ0]});Q97=makeQuery(id+"F0.imprint","IMPRINT",FACE,{"disambiguationData":[TD([[makeQuery(id+"F0.imprint","IMPRINT",EDGE,{"disambiguationData":[TD([[subQ2,-1.0]])],"derivedFrom":subQ1}),1.0]])]});}
            var Q98;
            {var subQ0=sQuery(id+"F0.wireOp",EDGE,"E26");var subQ1=sQuery(id+"F0.wireOp",EDGE,"E17");var subQ2=makeQuery(id+"F0.imprint","INTERSECT",VERTEX,{"derivedFrom":[subQ1,subQ0]});Q98=makeQuery(id+"F0.imprint","IMPRINT",FACE,{"disambiguationData":[TD([[makeQuery(id+"F0.imprint","IMPRINT",EDGE,{"disambiguationData":[TD([[subQ2,-1.0]])],"derivedFrom":subQ1}),1.0]])]});}
            var Q99;
            {var subQ0=sQuery(id+"F0.wireOp",EDGE,"E32");var subQ1=sQuery(id+"F0.wireOp",EDGE,"E15");var subQ2=makeQuery(id+"F0.imprint","INTERSECT",VERTEX,{"derivedFrom":[subQ1,subQ0]});Q99=makeQuery(id+"F0.imprint","IMPRINT",FACE,{"disambiguationData":[TD([[makeQuery(id+"F0.imprint","IMPRINT",EDGE,{"disambiguationData":[TD([[subQ2,-1.0]])],"derivedFrom":subQ1}),1.0]])]});}
            var Q100;
            {var subQ0=sQuery(id+"F0.wireOp",EDGE,"E23");var subQ1=sQuery(id+"F0.wireOp",EDGE,"E8");var subQ2=makeQuery(id+"F0.imprint","INTERSECT",VERTEX,{"derivedFrom":[subQ1,subQ0]});Q100=makeQuery(id+"F0.imprint","IMPRINT",FACE,{"disambiguationData":[TD([[makeQuery(id+"F0.imprint","IMPRINT",EDGE,{"disambiguationData":[TD([[subQ2,-1.0]])],"derivedFrom":subQ1}),1.0]])]});}
            var Q101;
            {var subQ0=sQuery(id+"F0.wireOp",EDGE,"E25");var subQ1=sQuery(id+"F0.wireOp",EDGE,"E12");var subQ2=makeQuery(id+"F0.imprint","INTERSECT",VERTEX,{"derivedFrom":[subQ1,subQ0]});Q101=makeQuery(id+"F0.imprint","IMPRINT",FACE,{"disambiguationData":[TD([[makeQuery(id+"F0.imprint","IMPRINT",EDGE,{"disambiguationData":[TD([[subQ2,-1.0]])],"derivedFrom":subQ1}),1.0]])]});}
            var Q102;
            {var subQ0=sQuery(id+"F0.wireOp",EDGE,"E26");var subQ1=sQuery(id+"F0.wireOp",EDGE,"E7");var subQ2=makeQuery(id+"F0.imprint","INTERSECT",VERTEX,{"derivedFrom":[subQ1,subQ0]});Q102=makeQuery(id+"F0.imprint","IMPRINT",FACE,{"disambiguationData":[TD([[makeQuery(id+"F0.imprint","IMPRINT",EDGE,{"disambiguationData":[TD([[subQ2,-1.0]])],"derivedFrom":subQ1}),1.0]])]});}
            var Q103;
            {var subQ0=sQuery(id+"F0.wireOp",EDGE,"E22");var subQ1=sQuery(id+"F0.wireOp",EDGE,"E6");var subQ2=makeQuery(id+"F0.imprint","INTERSECT",VERTEX,{"derivedFrom":[subQ1,subQ0]});Q103=makeQuery(id+"F0.imprint","IMPRINT",FACE,{"disambiguationData":[TD([[makeQuery(id+"F0.imprint","IMPRINT",EDGE,{"disambiguationData":[TD([[subQ2,-1.0]])],"derivedFrom":subQ1}),1.0]])]});}
            var Q104;
            {var subQ0=sQuery(id+"F0.wireOp",EDGE,"E33");var subQ1=sQuery(id+"F0.wireOp",EDGE,"E2");var subQ2=makeQuery(id+"F0.imprint","INTERSECT",VERTEX,{"derivedFrom":[subQ1,subQ0]});Q104=makeQuery(id+"F0.imprint","IMPRINT",FACE,{"disambiguationData":[TD([[makeQuery(id+"F0.imprint","IMPRINT",EDGE,{"disambiguationData":[TD([[subQ2,-1.0]])],"derivedFrom":subQ1}),1.0]])]});}
            var Q105;
            {var subQ0=sQuery(id+"F0.wireOp",EDGE,"E21");var subQ1=sQuery(id+"F0.wireOp",EDGE,"E8");var subQ2=makeQuery(id+"F0.imprint","INTERSECT",VERTEX,{"derivedFrom":[subQ1,subQ0]});Q105=makeQuery(id+"F0.imprint","IMPRINT",FACE,{"disambiguationData":[TD([[makeQuery(id+"F0.imprint","IMPRINT",EDGE,{"disambiguationData":[TD([[subQ2,-1.0]])],"derivedFrom":subQ1}),1.0]])]});}
            var Q106;
            {var subQ0=sQuery(id+"F0.wireOp",EDGE,"E22");var subQ1=sQuery(id+"F0.wireOp",EDGE,"E11");var subQ2=makeQuery(id+"F0.imprint","INTERSECT",VERTEX,{"derivedFrom":[subQ1,subQ0]});Q106=makeQuery(id+"F0.imprint","IMPRINT",FACE,{"disambiguationData":[TD([[makeQuery(id+"F0.imprint","IMPRINT",EDGE,{"disambiguationData":[TD([[subQ2,-1.0]])],"derivedFrom":subQ1}),1.0]])]});}
            var Q107;
            {var subQ0=sQuery(id+"F0.wireOp",EDGE,"E32");var subQ1=sQuery(id+"F0.wireOp",EDGE,"E13");var subQ2=makeQuery(id+"F0.imprint","INTERSECT",VERTEX,{"derivedFrom":[subQ1,subQ0]});Q107=makeQuery(id+"F0.imprint","IMPRINT",FACE,{"disambiguationData":[TD([[makeQuery(id+"F0.imprint","IMPRINT",EDGE,{"disambiguationData":[TD([[subQ2,-1.0]])],"derivedFrom":subQ1}),1.0]])]});}
            var Q108;
            {var subQ0=sQuery(id+"F0.wireOp",EDGE,"E21");var subQ1=sQuery(id+"F0.wireOp",EDGE,"E14");var subQ2=makeQuery(id+"F0.imprint","INTERSECT",VERTEX,{"derivedFrom":[subQ1,subQ0]});Q108=makeQuery(id+"F0.imprint","IMPRINT",FACE,{"disambiguationData":[TD([[makeQuery(id+"F0.imprint","IMPRINT",EDGE,{"disambiguationData":[TD([[subQ2,-1.0]])],"derivedFrom":subQ1}),1.0]])]});}
            var Q109;
            {var subQ0=sQuery(id+"F0.wireOp",EDGE,"E29");var subQ1=sQuery(id+"F0.wireOp",EDGE,"E6");var subQ2=makeQuery(id+"F0.imprint","INTERSECT",VERTEX,{"derivedFrom":[subQ1,subQ0]});Q109=makeQuery(id+"F0.imprint","IMPRINT",FACE,{"disambiguationData":[TD([[makeQuery(id+"F0.imprint","IMPRINT",EDGE,{"disambiguationData":[TD([[subQ2,-1.0]])],"derivedFrom":subQ1}),1.0]])]});}
            var Q110;
            {var subQ0=sQuery(id+"F0.wireOp",EDGE,"E30");var subQ1=sQuery(id+"F0.wireOp",EDGE,"E1");var subQ2=makeQuery(id+"F0.imprint","INTERSECT",VERTEX,{"derivedFrom":[subQ1,subQ0]});Q110=makeQuery(id+"F0.imprint","IMPRINT",FACE,{"disambiguationData":[TD([[makeQuery(id+"F0.imprint","IMPRINT",EDGE,{"disambiguationData":[TD([[subQ2,-1.0]])],"derivedFrom":subQ1}),1.0]])]});}
            var Q111;
            {var subQ0=sQuery(id+"F0.wireOp",EDGE,"E35");var subQ1=sQuery(id+"F0.wireOp",EDGE,"E6");var subQ2=makeQuery(id+"F0.imprint","INTERSECT",VERTEX,{"derivedFrom":[subQ1,subQ0]});Q111=makeQuery(id+"F0.imprint","IMPRINT",FACE,{"disambiguationData":[TD([[makeQuery(id+"F0.imprint","IMPRINT",EDGE,{"disambiguationData":[TD([[subQ2,-1.0]])],"derivedFrom":subQ1}),1.0]])]});}
            var Q112;
            {var subQ0=sQuery(id+"F0.wireOp",EDGE,"E19");var subQ1=sQuery(id+"F0.wireOp",EDGE,"E6");var subQ2=makeQuery(id+"F0.imprint","INTERSECT",VERTEX,{"derivedFrom":[subQ1,subQ0]});Q112=makeQuery(id+"F0.imprint","IMPRINT",FACE,{"disambiguationData":[TD([[makeQuery(id+"F0.imprint","IMPRINT",EDGE,{"disambiguationData":[TD([[subQ2,-1.0]])],"derivedFrom":subQ1}),1.0]])]});}
            var Q113;
            {var subQ0=sQuery(id+"F0.wireOp",EDGE,"E30");var subQ1=sQuery(id+"F0.wireOp",EDGE,"E8");var subQ2=makeQuery(id+"F0.imprint","INTERSECT",VERTEX,{"derivedFrom":[subQ1,subQ0]});Q113=makeQuery(id+"F0.imprint","IMPRINT",FACE,{"disambiguationData":[TD([[makeQuery(id+"F0.imprint","IMPRINT",EDGE,{"disambiguationData":[TD([[subQ2,-1.0]])],"derivedFrom":subQ1}),1.0]])]});}
            var Q114;
            {var subQ0=sQuery(id+"F0.wireOp",EDGE,"E30");var subQ1=sQuery(id+"F0.wireOp",EDGE,"E2");var subQ2=makeQuery(id+"F0.imprint","INTERSECT",VERTEX,{"derivedFrom":[subQ1,subQ0]});Q114=makeQuery(id+"F0.imprint","IMPRINT",FACE,{"disambiguationData":[TD([[makeQuery(id+"F0.imprint","IMPRINT",EDGE,{"disambiguationData":[TD([[subQ2,-1.0]])],"derivedFrom":subQ1}),1.0]])]});}
            var Q115;
            {var subQ0=sQuery(id+"F0.wireOp",EDGE,"E26");var subQ1=sQuery(id+"F0.wireOp",EDGE,"E2");var subQ2=makeQuery(id+"F0.imprint","INTERSECT",VERTEX,{"derivedFrom":[subQ1,subQ0]});Q115=makeQuery(id+"F0.imprint","IMPRINT",FACE,{"disambiguationData":[TD([[makeQuery(id+"F0.imprint","IMPRINT",EDGE,{"disambiguationData":[TD([[subQ2,-1.0]])],"derivedFrom":subQ1}),1.0]])]});}
            var Q116;
            {var subQ0=sQuery(id+"F0.wireOp",EDGE,"E21");var subQ1=sQuery(id+"F0.wireOp",EDGE,"E2");var subQ2=makeQuery(id+"F0.imprint","INTERSECT",VERTEX,{"derivedFrom":[subQ1,subQ0]});Q116=makeQuery(id+"F0.imprint","IMPRINT",FACE,{"disambiguationData":[TD([[makeQuery(id+"F0.imprint","IMPRINT",EDGE,{"disambiguationData":[TD([[subQ2,-1.0]])],"derivedFrom":subQ1}),1.0]])]});}
            var Q117;
            {var subQ0=sQuery(id+"F0.wireOp",EDGE,"E27");var subQ1=sQuery(id+"F0.wireOp",EDGE,"E6");var subQ2=makeQuery(id+"F0.imprint","INTERSECT",VERTEX,{"derivedFrom":[subQ1,subQ0]});Q117=makeQuery(id+"F0.imprint","IMPRINT",FACE,{"disambiguationData":[TD([[makeQuery(id+"F0.imprint","IMPRINT",EDGE,{"disambiguationData":[TD([[subQ2,-1.0]])],"derivedFrom":subQ1}),1.0]])]});}
            var Q118;
            {var subQ0=sQuery(id+"F0.wireOp",EDGE,"E19");var subQ1=sQuery(id+"F0.wireOp",EDGE,"E8");var subQ2=makeQuery(id+"F0.imprint","INTERSECT",VERTEX,{"derivedFrom":[subQ1,subQ0]});Q118=makeQuery(id+"F0.imprint","IMPRINT",FACE,{"disambiguationData":[TD([[makeQuery(id+"F0.imprint","IMPRINT",EDGE,{"disambiguationData":[TD([[subQ2,-1.0]])],"derivedFrom":subQ1}),1.0]])]});}
            var Q119;
            {var subQ0=sQuery(id+"F0.wireOp",EDGE,"E30");var subQ1=sQuery(id+"F0.wireOp",EDGE,"E16");var subQ2=makeQuery(id+"F0.imprint","INTERSECT",VERTEX,{"derivedFrom":[subQ1,subQ0]});Q119=makeQuery(id+"F0.imprint","IMPRINT",FACE,{"disambiguationData":[TD([[makeQuery(id+"F0.imprint","IMPRINT",EDGE,{"disambiguationData":[TD([[subQ2,-1.0]])],"derivedFrom":subQ1}),1.0]])]});}
            var Q120;
            {var subQ0=sQuery(id+"F0.wireOp",EDGE,"E24");var subQ1=sQuery(id+"F0.wireOp",EDGE,"E16");var subQ2=makeQuery(id+"F0.imprint","INTERSECT",VERTEX,{"derivedFrom":[subQ1,subQ0]});Q120=makeQuery(id+"F0.imprint","IMPRINT",FACE,{"disambiguationData":[TD([[makeQuery(id+"F0.imprint","IMPRINT",EDGE,{"disambiguationData":[TD([[subQ2,-1.0]])],"derivedFrom":subQ1}),1.0]])]});}
            var Q121;
            {var subQ0=sQuery(id+"F0.wireOp",EDGE,"E19");var subQ1=sQuery(id+"F0.wireOp",EDGE,"E12");var subQ2=makeQuery(id+"F0.imprint","INTERSECT",VERTEX,{"derivedFrom":[subQ1,subQ0]});Q121=makeQuery(id+"F0.imprint","IMPRINT",FACE,{"disambiguationData":[TD([[makeQuery(id+"F0.imprint","IMPRINT",EDGE,{"disambiguationData":[TD([[subQ2,-1.0]])],"derivedFrom":subQ1}),1.0]])]});}
            var Q122;
            {var subQ0=sQuery(id+"F0.wireOp",EDGE,"E22");var subQ1=sQuery(id+"F0.wireOp",EDGE,"E2");var subQ2=makeQuery(id+"F0.imprint","INTERSECT",VERTEX,{"derivedFrom":[subQ1,subQ0]});Q122=makeQuery(id+"F0.imprint","IMPRINT",FACE,{"disambiguationData":[TD([[makeQuery(id+"F0.imprint","IMPRINT",EDGE,{"disambiguationData":[TD([[subQ2,-1.0]])],"derivedFrom":subQ1}),1.0]])]});}
            var Q123;
            {var subQ0=sQuery(id+"F0.wireOp",EDGE,"E27");var subQ1=sQuery(id+"F0.wireOp",EDGE,"E8");var subQ2=makeQuery(id+"F0.imprint","INTERSECT",VERTEX,{"derivedFrom":[subQ1,subQ0]});Q123=makeQuery(id+"F0.imprint","IMPRINT",FACE,{"disambiguationData":[TD([[makeQuery(id+"F0.imprint","IMPRINT",EDGE,{"disambiguationData":[TD([[subQ2,-1.0]])],"derivedFrom":subQ1}),1.0]])]});}
            var Q124;
            {var subQ0=sQuery(id+"F0.wireOp",EDGE,"E22");var subQ1=sQuery(id+"F0.wireOp",EDGE,"E7");var subQ2=makeQuery(id+"F0.imprint","INTERSECT",VERTEX,{"derivedFrom":[subQ1,subQ0]});Q124=makeQuery(id+"F0.imprint","IMPRINT",FACE,{"disambiguationData":[TD([[makeQuery(id+"F0.imprint","IMPRINT",EDGE,{"disambiguationData":[TD([[subQ2,-1.0]])],"derivedFrom":subQ1}),1.0]])]});}
            var Q125;
            {var subQ0=sQuery(id+"F0.wireOp",EDGE,"E26");var subQ1=sQuery(id+"F0.wireOp",EDGE,"E10");var subQ2=makeQuery(id+"F0.imprint","INTERSECT",VERTEX,{"derivedFrom":[subQ1,subQ0]});Q125=makeQuery(id+"F0.imprint","IMPRINT",FACE,{"disambiguationData":[TD([[makeQuery(id+"F0.imprint","IMPRINT",EDGE,{"disambiguationData":[TD([[subQ2,-1.0]])],"derivedFrom":subQ1}),1.0]])]});}
            var Q126;
            {var subQ0=sQuery(id+"F0.wireOp",EDGE,"E25");var subQ1=sQuery(id+"F0.wireOp",EDGE,"E10");var subQ2=makeQuery(id+"F0.imprint","INTERSECT",VERTEX,{"derivedFrom":[subQ1,subQ0]});Q126=makeQuery(id+"F0.imprint","IMPRINT",FACE,{"disambiguationData":[TD([[makeQuery(id+"F0.imprint","IMPRINT",EDGE,{"disambiguationData":[TD([[subQ2,-1.0]])],"derivedFrom":subQ1}),1.0]])]});}
            var Q127;
            {var subQ0=sQuery(id+"F0.wireOp",EDGE,"E21");var subQ1=sQuery(id+"F0.wireOp",EDGE,"E6");var subQ2=makeQuery(id+"F0.imprint","INTERSECT",VERTEX,{"derivedFrom":[subQ1,subQ0]});Q127=makeQuery(id+"F0.imprint","IMPRINT",FACE,{"disambiguationData":[TD([[makeQuery(id+"F0.imprint","IMPRINT",EDGE,{"disambiguationData":[TD([[subQ2,-1.0]])],"derivedFrom":subQ1}),1.0]])]});}
            var Q128;
            {var subQ0=sQuery(id+"F0.wireOp",EDGE,"E29");var subQ1=sQuery(id+"F0.wireOp",EDGE,"E2");var subQ2=makeQuery(id+"F0.imprint","INTERSECT",VERTEX,{"derivedFrom":[subQ1,subQ0]});Q128=makeQuery(id+"F0.imprint","IMPRINT",FACE,{"disambiguationData":[TD([[makeQuery(id+"F0.imprint","IMPRINT",EDGE,{"disambiguationData":[TD([[subQ2,-1.0]])],"derivedFrom":subQ1}),1.0]])]});}
            var Q129;
            {var subQ0=sQuery(id+"F0.wireOp",EDGE,"E27");var subQ1=sQuery(id+"F0.wireOp",EDGE,"E12");var subQ2=makeQuery(id+"F0.imprint","INTERSECT",VERTEX,{"derivedFrom":[subQ1,subQ0]});Q129=makeQuery(id+"F0.imprint","IMPRINT",FACE,{"disambiguationData":[TD([[makeQuery(id+"F0.imprint","IMPRINT",EDGE,{"disambiguationData":[TD([[subQ2,-1.0]])],"derivedFrom":subQ1}),1.0]])]});}
            var Q130;
            {var subQ0=sQuery(id+"F0.wireOp",EDGE,"E32");var subQ1=sQuery(id+"F0.wireOp",EDGE,"E2");var subQ2=makeQuery(id+"F0.imprint","INTERSECT",VERTEX,{"derivedFrom":[subQ1,subQ0]});Q130=makeQuery(id+"F0.imprint","IMPRINT",FACE,{"disambiguationData":[TD([[makeQuery(id+"F0.imprint","IMPRINT",EDGE,{"disambiguationData":[TD([[subQ2,-1.0]])],"derivedFrom":subQ1}),1.0]])]});}
            var Q131;
            {var subQ0=sQuery(id+"F0.wireOp",EDGE,"E22");var subQ1=sQuery(id+"F0.wireOp",EDGE,"E12");var subQ2=makeQuery(id+"F0.imprint","INTERSECT",VERTEX,{"derivedFrom":[subQ1,subQ0]});Q131=makeQuery(id+"F0.imprint","IMPRINT",FACE,{"disambiguationData":[TD([[makeQuery(id+"F0.imprint","IMPRINT",EDGE,{"disambiguationData":[TD([[subQ2,-1.0]])],"derivedFrom":subQ1}),1.0]])]});}
            var Q132;
            {var subQ0=sQuery(id+"F0.wireOp",EDGE,"E23");var subQ1=sQuery(id+"F0.wireOp",EDGE,"E2");var subQ2=makeQuery(id+"F0.imprint","INTERSECT",VERTEX,{"derivedFrom":[subQ1,subQ0]});Q132=makeQuery(id+"F0.imprint","IMPRINT",FACE,{"disambiguationData":[TD([[makeQuery(id+"F0.imprint","IMPRINT",EDGE,{"disambiguationData":[TD([[subQ2,-1.0]])],"derivedFrom":subQ1}),1.0]])]});}
            var Q133;
            {var subQ0=sQuery(id+"F0.wireOp",EDGE,"E22");var subQ1=sQuery(id+"F0.wireOp",EDGE,"E10");var subQ2=makeQuery(id+"F0.imprint","INTERSECT",VERTEX,{"derivedFrom":[subQ1,subQ0]});Q133=makeQuery(id+"F0.imprint","IMPRINT",FACE,{"disambiguationData":[TD([[makeQuery(id+"F0.imprint","IMPRINT",EDGE,{"disambiguationData":[TD([[subQ2,-1.0]])],"derivedFrom":subQ1}),1.0]])]});}
            var Q134;
            {var subQ0=sQuery(id+"F0.wireOp",EDGE,"E26");var subQ1=sQuery(id+"F0.wireOp",EDGE,"E15");var subQ2=makeQuery(id+"F0.imprint","INTERSECT",VERTEX,{"derivedFrom":[subQ1,subQ0]});Q134=makeQuery(id+"F0.imprint","IMPRINT",FACE,{"disambiguationData":[TD([[makeQuery(id+"F0.imprint","IMPRINT",EDGE,{"disambiguationData":[TD([[subQ2,-1.0]])],"derivedFrom":subQ1}),1.0]])]});}
            var Q135;
            {var subQ0=sQuery(id+"F0.wireOp",EDGE,"E24");var subQ1=sQuery(id+"F0.wireOp",EDGE,"E14");var subQ2=makeQuery(id+"F0.imprint","INTERSECT",VERTEX,{"derivedFrom":[subQ1,subQ0]});Q135=makeQuery(id+"F0.imprint","IMPRINT",FACE,{"disambiguationData":[TD([[makeQuery(id+"F0.imprint","IMPRINT",EDGE,{"disambiguationData":[TD([[subQ2,-1.0]])],"derivedFrom":subQ1}),1.0]])]});}
            var Q136;
            {var subQ0=sQuery(id+"F0.wireOp",EDGE,"E24");var subQ1=sQuery(id+"F0.wireOp",EDGE,"E9");var subQ2=makeQuery(id+"F0.imprint","INTERSECT",VERTEX,{"derivedFrom":[subQ1,subQ0]});Q136=makeQuery(id+"F0.imprint","IMPRINT",FACE,{"disambiguationData":[TD([[makeQuery(id+"F0.imprint","IMPRINT",EDGE,{"disambiguationData":[TD([[subQ2,-1.0]])],"derivedFrom":subQ1}),1.0]])]});}
            var Q137;
            {var subQ0=sQuery(id+"F0.wireOp",EDGE,"E21");var subQ1=sQuery(id+"F0.wireOp",EDGE,"E12");var subQ2=makeQuery(id+"F0.imprint","INTERSECT",VERTEX,{"derivedFrom":[subQ1,subQ0]});Q137=makeQuery(id+"F0.imprint","IMPRINT",FACE,{"disambiguationData":[TD([[makeQuery(id+"F0.imprint","IMPRINT",EDGE,{"disambiguationData":[TD([[subQ2,-1.0]])],"derivedFrom":subQ1}),1.0]])]});}
            var Q138;
            {var subQ0=sQuery(id+"F0.wireOp",EDGE,"E22");var subQ1=sQuery(id+"F0.wireOp",EDGE,"E5");var subQ2=makeQuery(id+"F0.imprint","INTERSECT",VERTEX,{"derivedFrom":[subQ1,subQ0]});Q138=makeQuery(id+"F0.imprint","IMPRINT",FACE,{"disambiguationData":[TD([[makeQuery(id+"F0.imprint","IMPRINT",EDGE,{"disambiguationData":[TD([[subQ2,-1.0]])],"derivedFrom":subQ1}),1.0]])]});}
            var Q139;
            {var subQ0=sQuery(id+"F0.wireOp",EDGE,"E24");var subQ1=sQuery(id+"F0.wireOp",EDGE,"E15");var subQ2=makeQuery(id+"F0.imprint","INTERSECT",VERTEX,{"derivedFrom":[subQ1,subQ0]});Q139=makeQuery(id+"F0.imprint","IMPRINT",FACE,{"disambiguationData":[TD([[makeQuery(id+"F0.imprint","IMPRINT",EDGE,{"disambiguationData":[TD([[subQ2,-1.0]])],"derivedFrom":subQ1}),1.0]])]});}
            var Q140;
            {var subQ0=sQuery(id+"F0.wireOp",EDGE,"E24");var subQ1=sQuery(id+"F0.wireOp",EDGE,"E2");var subQ2=makeQuery(id+"F0.imprint","INTERSECT",VERTEX,{"derivedFrom":[subQ1,subQ0]});Q140=makeQuery(id+"F0.imprint","IMPRINT",FACE,{"disambiguationData":[TD([[makeQuery(id+"F0.imprint","IMPRINT",EDGE,{"disambiguationData":[TD([[subQ2,-1.0]])],"derivedFrom":subQ1}),1.0]])]});}
            var Q141;
            {var subQ0=sQuery(id+"F0.wireOp",EDGE,"E29");var subQ1=sQuery(id+"F0.wireOp",EDGE,"E14");var subQ2=makeQuery(id+"F0.imprint","INTERSECT",VERTEX,{"derivedFrom":[subQ1,subQ0]});Q141=makeQuery(id+"F0.imprint","IMPRINT",FACE,{"disambiguationData":[TD([[makeQuery(id+"F0.imprint","IMPRINT",EDGE,{"disambiguationData":[TD([[subQ2,-1.0]])],"derivedFrom":subQ1}),1.0]])]});}
            var Q142;
            {var subQ0=sQuery(id+"F0.wireOp",EDGE,"E31");var subQ1=sQuery(id+"F0.wireOp",EDGE,"E16");var subQ2=makeQuery(id+"F0.imprint","INTERSECT",VERTEX,{"derivedFrom":[subQ1,subQ0]});Q142=makeQuery(id+"F0.imprint","IMPRINT",FACE,{"disambiguationData":[TD([[makeQuery(id+"F0.imprint","IMPRINT",EDGE,{"disambiguationData":[TD([[subQ2,-1.0]])],"derivedFrom":subQ1}),1.0]])]});}
            var Q143;
            {var subQ0=sQuery(id+"F0.wireOp",EDGE,"E34");var subQ1=sQuery(id+"F0.wireOp",EDGE,"E15");var subQ2=makeQuery(id+"F0.imprint","INTERSECT",VERTEX,{"derivedFrom":[subQ1,subQ0]});Q143=makeQuery(id+"F0.imprint","IMPRINT",FACE,{"disambiguationData":[TD([[makeQuery(id+"F0.imprint","IMPRINT",EDGE,{"disambiguationData":[TD([[subQ2,-1.0]])],"derivedFrom":subQ1}),1.0]])]});}
            var Q144;
            {var subQ0=sQuery(id+"F0.wireOp",EDGE,"E25");var subQ1=sQuery(id+"F0.wireOp",EDGE,"E4");var subQ2=makeQuery(id+"F0.imprint","INTERSECT",VERTEX,{"derivedFrom":[subQ1,subQ0]});Q144=makeQuery(id+"F0.imprint","IMPRINT",FACE,{"disambiguationData":[TD([[makeQuery(id+"F0.imprint","IMPRINT",EDGE,{"disambiguationData":[TD([[subQ2,-1.0]])],"derivedFrom":subQ1}),1.0]])]});}
            var Q145;
            {var subQ0=sQuery(id+"F0.wireOp",EDGE,"E20");var subQ1=sQuery(id+"F0.wireOp",EDGE,"E6");var subQ2=makeQuery(id+"F0.imprint","INTERSECT",VERTEX,{"derivedFrom":[subQ1,subQ0]});Q145=makeQuery(id+"F0.imprint","IMPRINT",FACE,{"disambiguationData":[TD([[makeQuery(id+"F0.imprint","IMPRINT",EDGE,{"disambiguationData":[TD([[subQ2,-1.0]])],"derivedFrom":subQ1}),1.0]])]});}
            var Q146;
            {var subQ0=sQuery(id+"F0.wireOp",EDGE,"E22");var subQ1=sQuery(id+"F0.wireOp",EDGE,"E0.right");var subQ2=makeQuery(id+"F0.imprint","INTERSECT",VERTEX,{"derivedFrom":[subQ1,subQ0]});Q146=makeQuery(id+"F0.imprint","IMPRINT",FACE,{"disambiguationData":[TD([[makeQuery(id+"F0.imprint","IMPRINT",EDGE,{"disambiguationData":[TD([[subQ2,-1.0]])],"derivedFrom":subQ1}),-1.0]])]});}
            var Q147;
            {var subQ0=sQuery(id+"F0.wireOp",EDGE,"E7");var subQ1=sQuery(id+"F0.wireOp",EDGE,"E0.bottom");var subQ2=makeQuery(id+"F0.imprint","INTERSECT",VERTEX,{"derivedFrom":[subQ1,subQ0]});Q147=makeQuery(id+"F0.imprint","IMPRINT",FACE,{"disambiguationData":[TD([[makeQuery(id+"F0.imprint","IMPRINT",EDGE,{"disambiguationData":[TD([[subQ2,-1.0]])],"derivedFrom":subQ1}),-1.0]])]});}
            var Q148;
            {var subQ0=sQuery(id+"F0.wireOp",EDGE,"E20");var subQ1=sQuery(id+"F0.wireOp",EDGE,"E15");var subQ2=makeQuery(id+"F0.imprint","INTERSECT",VERTEX,{"derivedFrom":[subQ1,subQ0]});Q148=makeQuery(id+"F0.imprint","IMPRINT",FACE,{"disambiguationData":[TD([[makeQuery(id+"F0.imprint","IMPRINT",EDGE,{"disambiguationData":[TD([[subQ2,-1.0]])],"derivedFrom":subQ1}),1.0]])]});}
            var Q149;
            {var subQ0=sQuery(id+"F0.wireOp",EDGE,"E30");var subQ1=sQuery(id+"F0.wireOp",EDGE,"E0.left");var subQ2=makeQuery(id+"F0.imprint","INTERSECT",VERTEX,{"derivedFrom":[subQ1,subQ0]});Q149=makeQuery(id+"F0.imprint","IMPRINT",FACE,{"disambiguationData":[TD([[makeQuery(id+"F0.imprint","IMPRINT",EDGE,{"disambiguationData":[TD([[subQ2,-1.0]])],"derivedFrom":subQ1}),1.0]])]});}
            var Q150;
            {var subQ0=sQuery(id+"F0.wireOp",EDGE,"E20");var subQ1=sQuery(id+"F0.wireOp",EDGE,"E1");var subQ2=makeQuery(id+"F0.imprint","INTERSECT",VERTEX,{"derivedFrom":[subQ1,subQ0]});Q150=makeQuery(id+"F0.imprint","IMPRINT",FACE,{"disambiguationData":[TD([[makeQuery(id+"F0.imprint","IMPRINT",EDGE,{"disambiguationData":[TD([[subQ2,-1.0]])],"derivedFrom":subQ1}),1.0]])]});}
            var Q151;
            {var subQ0=sQuery(id+"F0.wireOp",EDGE,"E28");var subQ1=sQuery(id+"F0.wireOp",EDGE,"E12");var subQ2=makeQuery(id+"F0.imprint","INTERSECT",VERTEX,{"derivedFrom":[subQ1,subQ0]});Q151=makeQuery(id+"F0.imprint","IMPRINT",FACE,{"disambiguationData":[TD([[makeQuery(id+"F0.imprint","IMPRINT",EDGE,{"disambiguationData":[TD([[subQ2,-1.0]])],"derivedFrom":subQ1}),1.0]])]});}
            var Q152;
            {var subQ0=sQuery(id+"F0.wireOp",EDGE,"E35");var subQ1=sQuery(id+"F0.wireOp",EDGE,"E0.left");var subQ2=makeQuery(id+"F0.imprint","INTERSECT",VERTEX,{"derivedFrom":[subQ1,subQ0]});Q152=makeQuery(id+"F0.imprint","IMPRINT",FACE,{"disambiguationData":[TD([[makeQuery(id+"F0.imprint","IMPRINT",EDGE,{"disambiguationData":[TD([[subQ2,-1.0]])],"derivedFrom":subQ1}),1.0]])]});}
            var Q153;
            {var subQ0=sQuery(id+"F0.wireOp",EDGE,"E34");var subQ1=sQuery(id+"F0.wireOp",EDGE,"E17");var subQ2=makeQuery(id+"F0.imprint","INTERSECT",VERTEX,{"derivedFrom":[subQ1,subQ0]});Q153=makeQuery(id+"F0.imprint","IMPRINT",FACE,{"disambiguationData":[TD([[makeQuery(id+"F0.imprint","IMPRINT",EDGE,{"disambiguationData":[TD([[subQ2,-1.0]])],"derivedFrom":subQ1}),1.0]])]});}
            var Q154;
            {var subQ0=sQuery(id+"F0.wireOp",EDGE,"E28");var subQ1=sQuery(id+"F0.wireOp",EDGE,"E11");var subQ2=makeQuery(id+"F0.imprint","INTERSECT",VERTEX,{"derivedFrom":[subQ1,subQ0]});Q154=makeQuery(id+"F0.imprint","IMPRINT",FACE,{"disambiguationData":[TD([[makeQuery(id+"F0.imprint","IMPRINT",EDGE,{"disambiguationData":[TD([[subQ2,-1.0]])],"derivedFrom":subQ1}),1.0]])]});}
            var Q155;
            {var subQ0=sQuery(id+"F0.wireOp",EDGE,"E35");var subQ1=sQuery(id+"F0.wireOp",EDGE,"E0.right");var subQ2=makeQuery(id+"F0.imprint","INTERSECT",VERTEX,{"derivedFrom":[subQ1,subQ0]});Q155=makeQuery(id+"F0.imprint","IMPRINT",FACE,{"disambiguationData":[TD([[makeQuery(id+"F0.imprint","IMPRINT",EDGE,{"disambiguationData":[TD([[subQ2,-1.0]])],"derivedFrom":subQ1}),-1.0]])]});}
            var Q156;
            {var subQ0=sQuery(id+"F0.wireOp",EDGE,"E28");var subQ1=sQuery(id+"F0.wireOp",EDGE,"E10");var subQ2=makeQuery(id+"F0.imprint","INTERSECT",VERTEX,{"derivedFrom":[subQ1,subQ0]});Q156=makeQuery(id+"F0.imprint","IMPRINT",FACE,{"disambiguationData":[TD([[makeQuery(id+"F0.imprint","IMPRINT",EDGE,{"disambiguationData":[TD([[subQ2,-1.0]])],"derivedFrom":subQ1}),1.0]])]});}
            var Q157;
            {var subQ0=sQuery(id+"F0.wireOp",EDGE,"E24");var subQ1=sQuery(id+"F0.wireOp",EDGE,"E4");var subQ2=makeQuery(id+"F0.imprint","INTERSECT",VERTEX,{"derivedFrom":[subQ1,subQ0]});Q157=makeQuery(id+"F0.imprint","IMPRINT",FACE,{"disambiguationData":[TD([[makeQuery(id+"F0.imprint","IMPRINT",EDGE,{"disambiguationData":[TD([[subQ2,-1.0]])],"derivedFrom":subQ1}),1.0]])]});}
            var Q158;
            {var subQ0=sQuery(id+"F0.wireOp",EDGE,"E17");var subQ1=sQuery(id+"F0.wireOp",EDGE,"E0.bottom");var subQ2=makeQuery(id+"F0.imprint","INTERSECT",VERTEX,{"derivedFrom":[subQ1,subQ0]});Q158=makeQuery(id+"F0.imprint","IMPRINT",FACE,{"disambiguationData":[TD([[makeQuery(id+"F0.imprint","IMPRINT",EDGE,{"disambiguationData":[TD([[subQ2,-1.0]])],"derivedFrom":subQ1}),-1.0]])]});}
            var Q159;
            {var subQ0=sQuery(id+"F0.wireOp",EDGE,"E13");var subQ1=sQuery(id+"F0.wireOp",EDGE,"E0.bottom");var subQ2=makeQuery(id+"F0.imprint","INTERSECT",VERTEX,{"derivedFrom":[subQ1,subQ0]});Q159=makeQuery(id+"F0.imprint","IMPRINT",FACE,{"disambiguationData":[TD([[makeQuery(id+"F0.imprint","IMPRINT",EDGE,{"disambiguationData":[TD([[subQ2,-1.0]])],"derivedFrom":subQ1}),-1.0]])]});}
            var Q160;
            {var subQ0=sQuery(id+"F0.wireOp",EDGE,"E20");var subQ1=sQuery(id+"F0.wireOp",EDGE,"E5");var subQ2=makeQuery(id+"F0.imprint","INTERSECT",VERTEX,{"derivedFrom":[subQ1,subQ0]});Q160=makeQuery(id+"F0.imprint","IMPRINT",FACE,{"disambiguationData":[TD([[makeQuery(id+"F0.imprint","IMPRINT",EDGE,{"disambiguationData":[TD([[subQ2,-1.0]])],"derivedFrom":subQ1}),1.0]])]});}
            var Q161;
            {var subQ0=sQuery(id+"F0.wireOp",EDGE,"E20");var subQ1=sQuery(id+"F0.wireOp",EDGE,"E16");var subQ2=makeQuery(id+"F0.imprint","INTERSECT",VERTEX,{"derivedFrom":[subQ1,subQ0]});Q161=makeQuery(id+"F0.imprint","IMPRINT",FACE,{"disambiguationData":[TD([[makeQuery(id+"F0.imprint","IMPRINT",EDGE,{"disambiguationData":[TD([[subQ2,-1.0]])],"derivedFrom":subQ1}),1.0]])]});}
            var Q162;
            {var subQ0=sQuery(id+"F0.wireOp",EDGE,"E16");var subQ1=sQuery(id+"F0.wireOp",EDGE,"E0.bottom");var subQ2=makeQuery(id+"F0.imprint","INTERSECT",VERTEX,{"derivedFrom":[subQ1,subQ0]});Q162=makeQuery(id+"F0.imprint","IMPRINT",FACE,{"disambiguationData":[TD([[makeQuery(id+"F0.imprint","IMPRINT",EDGE,{"disambiguationData":[TD([[subQ2,-1.0]])],"derivedFrom":subQ1}),-1.0]])]});}
            var Q163;
            {var subQ0=sQuery(id+"F0.wireOp",EDGE,"E33");var subQ1=sQuery(id+"F0.wireOp",EDGE,"E0.right");var subQ2=makeQuery(id+"F0.imprint","INTERSECT",VERTEX,{"derivedFrom":[subQ1,subQ0]});Q163=makeQuery(id+"F0.imprint","IMPRINT",FACE,{"disambiguationData":[TD([[makeQuery(id+"F0.imprint","IMPRINT",EDGE,{"disambiguationData":[TD([[subQ2,-1.0]])],"derivedFrom":subQ1}),-1.0]])]});}
            var Q164;
            {var subQ0=sQuery(id+"F0.wireOp",EDGE,"E28");var subQ1=sQuery(id+"F0.wireOp",EDGE,"E3");var subQ2=makeQuery(id+"F0.imprint","INTERSECT",VERTEX,{"derivedFrom":[subQ1,subQ0]});Q164=makeQuery(id+"F0.imprint","IMPRINT",FACE,{"disambiguationData":[TD([[makeQuery(id+"F0.imprint","IMPRINT",EDGE,{"disambiguationData":[TD([[subQ2,-1.0]])],"derivedFrom":subQ1}),1.0]])]});}
            var Q165;
            {var subQ0=sQuery(id+"F0.wireOp",EDGE,"E28");var subQ1=sQuery(id+"F0.wireOp",EDGE,"E6");var subQ2=makeQuery(id+"F0.imprint","INTERSECT",VERTEX,{"derivedFrom":[subQ1,subQ0]});Q165=makeQuery(id+"F0.imprint","IMPRINT",FACE,{"disambiguationData":[TD([[makeQuery(id+"F0.imprint","IMPRINT",EDGE,{"disambiguationData":[TD([[subQ2,-1.0]])],"derivedFrom":subQ1}),1.0]])]});}
            var Q166;
            {var subQ0=sQuery(id+"F0.wireOp",EDGE,"E28");var subQ1=sQuery(id+"F0.wireOp",EDGE,"E1");var subQ2=makeQuery(id+"F0.imprint","INTERSECT",VERTEX,{"derivedFrom":[subQ1,subQ0]});Q166=makeQuery(id+"F0.imprint","IMPRINT",FACE,{"disambiguationData":[TD([[makeQuery(id+"F0.imprint","IMPRINT",EDGE,{"disambiguationData":[TD([[subQ2,-1.0]])],"derivedFrom":subQ1}),1.0]])]});}
            var Q167;
            {var subQ0=sQuery(id+"F0.wireOp",EDGE,"E20");var subQ1=sQuery(id+"F0.wireOp",EDGE,"E10");var subQ2=makeQuery(id+"F0.imprint","INTERSECT",VERTEX,{"derivedFrom":[subQ1,subQ0]});Q167=makeQuery(id+"F0.imprint","IMPRINT",FACE,{"disambiguationData":[TD([[makeQuery(id+"F0.imprint","IMPRINT",EDGE,{"disambiguationData":[TD([[subQ2,-1.0]])],"derivedFrom":subQ1}),1.0]])]});}
            var Q168;
            {var subQ0=sQuery(id+"F0.wireOp",EDGE,"E20");var subQ1=sQuery(id+"F0.wireOp",EDGE,"E14");var subQ2=makeQuery(id+"F0.imprint","INTERSECT",VERTEX,{"derivedFrom":[subQ1,subQ0]});Q168=makeQuery(id+"F0.imprint","IMPRINT",FACE,{"disambiguationData":[TD([[makeQuery(id+"F0.imprint","IMPRINT",EDGE,{"disambiguationData":[TD([[subQ2,-1.0]])],"derivedFrom":subQ1}),1.0]])]});}
            var Q169;
            {var subQ0=sQuery(id+"F0.wireOp",EDGE,"E4");var subQ1=sQuery(id+"F0.wireOp",EDGE,"E0.bottom");var subQ2=makeQuery(id+"F0.imprint","INTERSECT",VERTEX,{"derivedFrom":[subQ1,subQ0]});Q169=makeQuery(id+"F0.imprint","IMPRINT",FACE,{"disambiguationData":[TD([[makeQuery(id+"F0.imprint","IMPRINT",EDGE,{"disambiguationData":[TD([[subQ2,-1.0]])],"derivedFrom":subQ1}),-1.0]])]});}
            var Q170;
            {var subQ0=sQuery(id+"F0.wireOp",EDGE,"E14");var subQ1=sQuery(id+"F0.wireOp",EDGE,"E0.bottom");var subQ2=makeQuery(id+"F0.imprint","INTERSECT",VERTEX,{"derivedFrom":[subQ1,subQ0]});Q170=makeQuery(id+"F0.imprint","IMPRINT",FACE,{"disambiguationData":[TD([[makeQuery(id+"F0.imprint","IMPRINT",EDGE,{"disambiguationData":[TD([[subQ2,-1.0]])],"derivedFrom":subQ1}),-1.0]])]});}
            var Q171;
            {var subQ0=sQuery(id+"F0.wireOp",EDGE,"E7");var subQ1=sQuery(id+"F0.wireOp",EDGE,"E0.top");var subQ2=makeQuery(id+"F0.imprint","INTERSECT",VERTEX,{"derivedFrom":[subQ1,subQ0]});Q171=makeQuery(id+"F0.imprint","IMPRINT",FACE,{"disambiguationData":[TD([[makeQuery(id+"F0.imprint","IMPRINT",EDGE,{"disambiguationData":[TD([[subQ2,-1.0]])],"derivedFrom":subQ1}),1.0]])]});}
            var Q172;
            {var subQ0=sQuery(id+"F0.wireOp",EDGE,"E30");var subQ1=sQuery(id+"F0.wireOp",EDGE,"E4");var subQ2=makeQuery(id+"F0.imprint","INTERSECT",VERTEX,{"derivedFrom":[subQ1,subQ0]});Q172=makeQuery(id+"F0.imprint","IMPRINT",FACE,{"disambiguationData":[TD([[makeQuery(id+"F0.imprint","IMPRINT",EDGE,{"disambiguationData":[TD([[subQ2,-1.0]])],"derivedFrom":subQ1}),1.0]])]});}
            var Q173;
            {var subQ0=sQuery(id+"F0.wireOp",EDGE,"E23");var subQ1=sQuery(id+"F0.wireOp",EDGE,"E0.right");var subQ2=makeQuery(id+"F0.imprint","INTERSECT",VERTEX,{"derivedFrom":[subQ1,subQ0]});Q173=makeQuery(id+"F0.imprint","IMPRINT",FACE,{"disambiguationData":[TD([[makeQuery(id+"F0.imprint","IMPRINT",EDGE,{"disambiguationData":[TD([[subQ2,-1.0]])],"derivedFrom":subQ1}),-1.0]])]});}
            var Q174;
            {var subQ0=sQuery(id+"F0.wireOp",EDGE,"E34");var subQ1=sQuery(id+"F0.wireOp",EDGE,"E16");var subQ2=makeQuery(id+"F0.imprint","INTERSECT",VERTEX,{"derivedFrom":[subQ1,subQ0]});Q174=makeQuery(id+"F0.imprint","IMPRINT",FACE,{"disambiguationData":[TD([[makeQuery(id+"F0.imprint","IMPRINT",EDGE,{"disambiguationData":[TD([[subQ2,-1.0]])],"derivedFrom":subQ1}),1.0]])]});}
            var Q175;
            {var subQ0=sQuery(id+"F0.wireOp",EDGE,"E32");var subQ1=sQuery(id+"F0.wireOp",EDGE,"E0.left");var subQ2=makeQuery(id+"F0.imprint","INTERSECT",VERTEX,{"derivedFrom":[subQ1,subQ0]});Q175=makeQuery(id+"F0.imprint","IMPRINT",FACE,{"disambiguationData":[TD([[makeQuery(id+"F0.imprint","IMPRINT",EDGE,{"disambiguationData":[TD([[subQ2,-1.0]])],"derivedFrom":subQ1}),1.0]])]});}
            var Q176;
            {var subQ0=sQuery(id+"F0.wireOp",EDGE,"E34");var subQ1=sQuery(id+"F0.wireOp",EDGE,"E7");var subQ2=makeQuery(id+"F0.imprint","INTERSECT",VERTEX,{"derivedFrom":[subQ1,subQ0]});Q176=makeQuery(id+"F0.imprint","IMPRINT",FACE,{"disambiguationData":[TD([[makeQuery(id+"F0.imprint","IMPRINT",EDGE,{"disambiguationData":[TD([[subQ2,-1.0]])],"derivedFrom":subQ1}),1.0]])]});}
            var Q177;
            {var subQ0=sQuery(id+"F0.wireOp",EDGE,"E22");var subQ1=sQuery(id+"F0.wireOp",EDGE,"E4");var subQ2=makeQuery(id+"F0.imprint","INTERSECT",VERTEX,{"derivedFrom":[subQ1,subQ0]});Q177=makeQuery(id+"F0.imprint","IMPRINT",FACE,{"disambiguationData":[TD([[makeQuery(id+"F0.imprint","IMPRINT",EDGE,{"disambiguationData":[TD([[subQ2,-1.0]])],"derivedFrom":subQ1}),1.0]])]});}
            var Q178;
            {var subQ0=sQuery(id+"F0.wireOp",EDGE,"E14");var subQ1=sQuery(id+"F0.wireOp",EDGE,"E0.top");var subQ2=makeQuery(id+"F0.imprint","INTERSECT",VERTEX,{"derivedFrom":[subQ1,subQ0]});Q178=makeQuery(id+"F0.imprint","IMPRINT",FACE,{"disambiguationData":[TD([[makeQuery(id+"F0.imprint","IMPRINT",EDGE,{"disambiguationData":[TD([[subQ2,-1.0]])],"derivedFrom":subQ1}),1.0]])]});}
            var Q179;
            {var subQ0=sQuery(id+"F0.wireOp",EDGE,"E34");var subQ1=sQuery(id+"F0.wireOp",EDGE,"E1");var subQ2=makeQuery(id+"F0.imprint","INTERSECT",VERTEX,{"derivedFrom":[subQ1,subQ0]});Q179=makeQuery(id+"F0.imprint","IMPRINT",FACE,{"disambiguationData":[TD([[makeQuery(id+"F0.imprint","IMPRINT",EDGE,{"disambiguationData":[TD([[subQ2,-1.0]])],"derivedFrom":subQ1}),1.0]])]});}
            var Q180;
            {var subQ0=sQuery(id+"F0.wireOp",EDGE,"E21");var subQ1=sQuery(id+"F0.wireOp",EDGE,"E0.right");var subQ2=makeQuery(id+"F0.imprint","INTERSECT",VERTEX,{"derivedFrom":[subQ1,subQ0]});Q180=makeQuery(id+"F0.imprint","IMPRINT",FACE,{"disambiguationData":[TD([[makeQuery(id+"F0.imprint","IMPRINT",EDGE,{"disambiguationData":[TD([[subQ2,-1.0]])],"derivedFrom":subQ1}),-1.0]])]});}
            var Q181;
            {var subQ0=sQuery(id+"F0.wireOp",EDGE,"E16");var subQ1=sQuery(id+"F0.wireOp",EDGE,"E0.top");var subQ2=makeQuery(id+"F0.imprint","INTERSECT",VERTEX,{"derivedFrom":[subQ1,subQ0]});Q181=makeQuery(id+"F0.imprint","IMPRINT",FACE,{"disambiguationData":[TD([[makeQuery(id+"F0.imprint","IMPRINT",EDGE,{"disambiguationData":[TD([[subQ2,-1.0]])],"derivedFrom":subQ1}),1.0]])]});}
            var Q182;
            {var subQ0=sQuery(id+"F0.wireOp",EDGE,"E31");var subQ1=sQuery(id+"F0.wireOp",EDGE,"E4");var subQ2=makeQuery(id+"F0.imprint","INTERSECT",VERTEX,{"derivedFrom":[subQ1,subQ0]});Q182=makeQuery(id+"F0.imprint","IMPRINT",FACE,{"disambiguationData":[TD([[makeQuery(id+"F0.imprint","IMPRINT",EDGE,{"disambiguationData":[TD([[subQ2,-1.0]])],"derivedFrom":subQ1}),1.0]])]});}
            var Q183;
            {var subQ0=sQuery(id+"F0.wireOp",EDGE,"E32");var subQ1=sQuery(id+"F0.wireOp",EDGE,"E4");var subQ2=makeQuery(id+"F0.imprint","INTERSECT",VERTEX,{"derivedFrom":[subQ1,subQ0]});Q183=makeQuery(id+"F0.imprint","IMPRINT",FACE,{"disambiguationData":[TD([[makeQuery(id+"F0.imprint","IMPRINT",EDGE,{"disambiguationData":[TD([[subQ2,-1.0]])],"derivedFrom":subQ1}),1.0]])]});}
            var Q184;
            {var subQ0=sQuery(id+"F0.wireOp",EDGE,"E33");var subQ1=sQuery(id+"F0.wireOp",EDGE,"E0.left");var subQ2=makeQuery(id+"F0.imprint","INTERSECT",VERTEX,{"derivedFrom":[subQ1,subQ0]});Q184=makeQuery(id+"F0.imprint","IMPRINT",FACE,{"disambiguationData":[TD([[makeQuery(id+"F0.imprint","IMPRINT",EDGE,{"disambiguationData":[TD([[subQ2,-1.0]])],"derivedFrom":subQ1}),1.0]])]});}
            var Q185;
            {var subQ0=sQuery(id+"F0.wireOp",EDGE,"E20");var subQ1=sQuery(id+"F0.wireOp",EDGE,"E3");var subQ2=makeQuery(id+"F0.imprint","INTERSECT",VERTEX,{"derivedFrom":[subQ1,subQ0]});Q185=makeQuery(id+"F0.imprint","IMPRINT",FACE,{"disambiguationData":[TD([[makeQuery(id+"F0.imprint","IMPRINT",EDGE,{"disambiguationData":[TD([[subQ2,-1.0]])],"derivedFrom":subQ1}),1.0]])]});}
            var Q186;
            {var subQ0=sQuery(id+"F0.wireOp",EDGE,"E20");var subQ1=sQuery(id+"F0.wireOp",EDGE,"E17");var subQ2=makeQuery(id+"F0.imprint","INTERSECT",VERTEX,{"derivedFrom":[subQ1,subQ0]});Q186=makeQuery(id+"F0.imprint","IMPRINT",FACE,{"disambiguationData":[TD([[makeQuery(id+"F0.imprint","IMPRINT",EDGE,{"disambiguationData":[TD([[subQ2,-1.0]])],"derivedFrom":subQ1}),1.0]])]});}
            var Q187;
            {var subQ0=sQuery(id+"F0.wireOp",EDGE,"E28");var subQ1=sQuery(id+"F0.wireOp",EDGE,"E13");var subQ2=makeQuery(id+"F0.imprint","INTERSECT",VERTEX,{"derivedFrom":[subQ1,subQ0]});Q187=makeQuery(id+"F0.imprint","IMPRINT",FACE,{"disambiguationData":[TD([[makeQuery(id+"F0.imprint","IMPRINT",EDGE,{"disambiguationData":[TD([[subQ2,-1.0]])],"derivedFrom":subQ1}),1.0]])]});}
            var Q188;
            {var subQ0=sQuery(id+"F0.wireOp",EDGE,"E35");var subQ1=sQuery(id+"F0.wireOp",EDGE,"E4");var subQ2=makeQuery(id+"F0.imprint","INTERSECT",VERTEX,{"derivedFrom":[subQ1,subQ0]});Q188=makeQuery(id+"F0.imprint","IMPRINT",FACE,{"disambiguationData":[TD([[makeQuery(id+"F0.imprint","IMPRINT",EDGE,{"disambiguationData":[TD([[subQ2,-1.0]])],"derivedFrom":subQ1}),1.0]])]});}
            var Q189;
            {var subQ0=sQuery(id+"F0.wireOp",EDGE,"E34");var subQ1=sQuery(id+"F0.wireOp",EDGE,"E11");var subQ2=makeQuery(id+"F0.imprint","INTERSECT",VERTEX,{"derivedFrom":[subQ1,subQ0]});Q189=makeQuery(id+"F0.imprint","IMPRINT",FACE,{"disambiguationData":[TD([[makeQuery(id+"F0.imprint","IMPRINT",EDGE,{"disambiguationData":[TD([[subQ2,-1.0]])],"derivedFrom":subQ1}),1.0]])]});}
            var Q190;
            {var subQ0=sQuery(id+"F0.wireOp",EDGE,"E11");var subQ1=sQuery(id+"F0.wireOp",EDGE,"E0.bottom");var subQ2=makeQuery(id+"F0.imprint","INTERSECT",VERTEX,{"derivedFrom":[subQ1,subQ0]});Q190=makeQuery(id+"F0.imprint","IMPRINT",FACE,{"disambiguationData":[TD([[makeQuery(id+"F0.imprint","IMPRINT",EDGE,{"disambiguationData":[TD([[subQ2,-1.0]])],"derivedFrom":subQ1}),-1.0]])]});}
            var Q191;
            {var subQ0=sQuery(id+"F0.wireOp",EDGE,"E23");var subQ1=sQuery(id+"F0.wireOp",EDGE,"E0.left");var subQ2=makeQuery(id+"F0.imprint","INTERSECT",VERTEX,{"derivedFrom":[subQ1,subQ0]});Q191=makeQuery(id+"F0.imprint","IMPRINT",FACE,{"disambiguationData":[TD([[makeQuery(id+"F0.imprint","IMPRINT",EDGE,{"disambiguationData":[TD([[subQ2,-1.0]])],"derivedFrom":subQ1}),1.0]])]});}
            var Q192;
            {var subQ0=sQuery(id+"F0.wireOp",EDGE,"E26");var subQ1=sQuery(id+"F0.wireOp",EDGE,"E0.left");var subQ2=makeQuery(id+"F0.imprint","INTERSECT",VERTEX,{"derivedFrom":[subQ1,subQ0]});Q192=makeQuery(id+"F0.imprint","IMPRINT",FACE,{"disambiguationData":[TD([[makeQuery(id+"F0.imprint","IMPRINT",EDGE,{"disambiguationData":[TD([[subQ2,-1.0]])],"derivedFrom":subQ1}),1.0]])]});}
            var Q193;
            {var subQ0=sQuery(id+"F0.wireOp",EDGE,"E24");var subQ1=sQuery(id+"F0.wireOp",EDGE,"E0.left");var subQ2=makeQuery(id+"F0.imprint","INTERSECT",VERTEX,{"derivedFrom":[subQ1,subQ0]});Q193=makeQuery(id+"F0.imprint","IMPRINT",FACE,{"disambiguationData":[TD([[makeQuery(id+"F0.imprint","IMPRINT",EDGE,{"disambiguationData":[TD([[subQ2,-1.0]])],"derivedFrom":subQ1}),1.0]])]});}
            var Q194;
            {var subQ0=sQuery(id+"F0.wireOp",EDGE,"E31");var subQ1=sQuery(id+"F0.wireOp",EDGE,"E0.left");var subQ2=makeQuery(id+"F0.imprint","INTERSECT",VERTEX,{"derivedFrom":[subQ1,subQ0]});Q194=makeQuery(id+"F0.imprint","IMPRINT",FACE,{"disambiguationData":[TD([[makeQuery(id+"F0.imprint","IMPRINT",EDGE,{"disambiguationData":[TD([[subQ2,-1.0]])],"derivedFrom":subQ1}),1.0]])]});}
            var Q195;
            {var subQ0=sQuery(id+"F0.wireOp",EDGE,"E20");var subQ1=sQuery(id+"F0.wireOp",EDGE,"E0.right");var subQ2=makeQuery(id+"F0.imprint","INTERSECT",VERTEX,{"derivedFrom":[subQ1,subQ0]});Q195=makeQuery(id+"F0.imprint","IMPRINT",FACE,{"disambiguationData":[TD([[makeQuery(id+"F0.imprint","IMPRINT",EDGE,{"disambiguationData":[TD([[subQ2,-1.0]])],"derivedFrom":subQ1}),-1.0]])]});}
            var Q196;
            {var subQ0=sQuery(id+"F0.wireOp",EDGE,"E8");var subQ1=sQuery(id+"F0.wireOp",EDGE,"E0.bottom");var subQ2=makeQuery(id+"F0.imprint","INTERSECT",VERTEX,{"derivedFrom":[subQ1,subQ0]});Q196=makeQuery(id+"F0.imprint","IMPRINT",FACE,{"disambiguationData":[TD([[makeQuery(id+"F0.imprint","IMPRINT",EDGE,{"disambiguationData":[TD([[subQ2,-1.0]])],"derivedFrom":subQ1}),-1.0]])]});}
            var Q197;
            {var subQ0=sQuery(id+"F0.wireOp",EDGE,"E30");var subQ1=sQuery(id+"F0.wireOp",EDGE,"E0.right");var subQ2=makeQuery(id+"F0.imprint","INTERSECT",VERTEX,{"derivedFrom":[subQ1,subQ0]});Q197=makeQuery(id+"F0.imprint","IMPRINT",FACE,{"disambiguationData":[TD([[makeQuery(id+"F0.imprint","IMPRINT",EDGE,{"disambiguationData":[TD([[subQ2,-1.0]])],"derivedFrom":subQ1}),-1.0]])]});}
            var Q198;
            {var subQ0=sQuery(id+"F0.wireOp",EDGE,"E20");var subQ1=sQuery(id+"F0.wireOp",EDGE,"E9");var subQ2=makeQuery(id+"F0.imprint","INTERSECT",VERTEX,{"derivedFrom":[subQ1,subQ0]});Q198=makeQuery(id+"F0.imprint","IMPRINT",FACE,{"disambiguationData":[TD([[makeQuery(id+"F0.imprint","IMPRINT",EDGE,{"disambiguationData":[TD([[subQ2,-1.0]])],"derivedFrom":subQ1}),1.0]])]});}
            var Q199;
            {var subQ0=sQuery(id+"F0.wireOp",EDGE,"E20");var subQ1=sQuery(id+"F0.wireOp",EDGE,"E4");var subQ2=makeQuery(id+"F0.imprint","INTERSECT",VERTEX,{"derivedFrom":[subQ1,subQ0]});Q199=makeQuery(id+"F0.imprint","IMPRINT",FACE,{"disambiguationData":[TD([[makeQuery(id+"F0.imprint","IMPRINT",EDGE,{"disambiguationData":[TD([[subQ2,-1.0]])],"derivedFrom":subQ1}),1.0]])]});}
            var Q200;
            {var subQ0=sQuery(id+"F0.wireOp",EDGE,"E19");var subQ1=sQuery(id+"F0.wireOp",EDGE,"E0.left");var subQ2=makeQuery(id+"F0.imprint","INTERSECT",VERTEX,{"derivedFrom":[subQ1,subQ0]});Q200=makeQuery(id+"F0.imprint","IMPRINT",FACE,{"disambiguationData":[TD([[makeQuery(id+"F0.imprint","IMPRINT",EDGE,{"disambiguationData":[TD([[subQ2,-1.0]])],"derivedFrom":subQ1}),1.0]])]});}
            var Q201;
            {var subQ0=sQuery(id+"F0.wireOp",EDGE,"E22");var subQ1=sQuery(id+"F0.wireOp",EDGE,"E0.left");var subQ2=makeQuery(id+"F0.imprint","INTERSECT",VERTEX,{"derivedFrom":[subQ1,subQ0]});Q201=makeQuery(id+"F0.imprint","IMPRINT",FACE,{"disambiguationData":[TD([[makeQuery(id+"F0.imprint","IMPRINT",EDGE,{"disambiguationData":[TD([[subQ2,-1.0]])],"derivedFrom":subQ1}),1.0]])]});}
            var Q202;
            {var subQ0=sQuery(id+"F0.wireOp",EDGE,"E34");var subQ1=sQuery(id+"F0.wireOp",EDGE,"E0.left");var subQ2=makeQuery(id+"F0.imprint","INTERSECT",VERTEX,{"derivedFrom":[subQ1,subQ0]});Q202=makeQuery(id+"F0.imprint","IMPRINT",FACE,{"disambiguationData":[TD([[makeQuery(id+"F0.imprint","IMPRINT",EDGE,{"disambiguationData":[TD([[subQ2,-1.0]])],"derivedFrom":subQ1}),1.0]])]});}
            var Q203;
            {var subQ0=sQuery(id+"F0.wireOp",EDGE,"E34");var subQ1=sQuery(id+"F0.wireOp",EDGE,"E10");var subQ2=makeQuery(id+"F0.imprint","INTERSECT",VERTEX,{"derivedFrom":[subQ1,subQ0]});Q203=makeQuery(id+"F0.imprint","IMPRINT",FACE,{"disambiguationData":[TD([[makeQuery(id+"F0.imprint","IMPRINT",EDGE,{"disambiguationData":[TD([[subQ2,-1.0]])],"derivedFrom":subQ1}),1.0]])]});}
            var Q204;
            {var subQ0=sQuery(id+"F0.wireOp",EDGE,"E20");var subQ1=sQuery(id+"F0.wireOp",EDGE,"E8");var subQ2=makeQuery(id+"F0.imprint","INTERSECT",VERTEX,{"derivedFrom":[subQ1,subQ0]});Q204=makeQuery(id+"F0.imprint","IMPRINT",FACE,{"disambiguationData":[TD([[makeQuery(id+"F0.imprint","IMPRINT",EDGE,{"disambiguationData":[TD([[subQ2,-1.0]])],"derivedFrom":subQ1}),1.0]])]});}
            var Q205;
            {var subQ0=sQuery(id+"F0.wireOp",EDGE,"E25");var subQ1=sQuery(id+"F0.wireOp",EDGE,"E0.left");var subQ2=makeQuery(id+"F0.imprint","INTERSECT",VERTEX,{"derivedFrom":[subQ1,subQ0]});Q205=makeQuery(id+"F0.imprint","IMPRINT",FACE,{"disambiguationData":[TD([[makeQuery(id+"F0.imprint","IMPRINT",EDGE,{"disambiguationData":[TD([[subQ2,-1.0]])],"derivedFrom":subQ1}),1.0]])]});}
            var Q206;
            {var subQ0=sQuery(id+"F0.wireOp",EDGE,"E26");var subQ1=sQuery(id+"F0.wireOp",EDGE,"E0.right");var subQ2=makeQuery(id+"F0.imprint","INTERSECT",VERTEX,{"derivedFrom":[subQ1,subQ0]});Q206=makeQuery(id+"F0.imprint","IMPRINT",FACE,{"disambiguationData":[TD([[makeQuery(id+"F0.imprint","IMPRINT",EDGE,{"disambiguationData":[TD([[subQ2,-1.0]])],"derivedFrom":subQ1}),-1.0]])]});}
            var Q207;
            {var subQ0=sQuery(id+"F0.wireOp",EDGE,"E20");var subQ1=sQuery(id+"F0.wireOp",EDGE,"E11");var subQ2=makeQuery(id+"F0.imprint","INTERSECT",VERTEX,{"derivedFrom":[subQ1,subQ0]});Q207=makeQuery(id+"F0.imprint","IMPRINT",FACE,{"disambiguationData":[TD([[makeQuery(id+"F0.imprint","IMPRINT",EDGE,{"disambiguationData":[TD([[subQ2,-1.0]])],"derivedFrom":subQ1}),1.0]])]});}
            var Q208;
            {var subQ0=sQuery(id+"F0.wireOp",EDGE,"E34");var subQ1=sQuery(id+"F0.wireOp",EDGE,"E12");var subQ2=makeQuery(id+"F0.imprint","INTERSECT",VERTEX,{"derivedFrom":[subQ1,subQ0]});Q208=makeQuery(id+"F0.imprint","IMPRINT",FACE,{"disambiguationData":[TD([[makeQuery(id+"F0.imprint","IMPRINT",EDGE,{"disambiguationData":[TD([[subQ2,-1.0]])],"derivedFrom":subQ1}),1.0]])]});}
            var Q209;
            {var subQ0=sQuery(id+"F0.wireOp",EDGE,"E1");var subQ1=sQuery(id+"F0.wireOp",EDGE,"E0.top");var subQ2=makeQuery(id+"F0.imprint","INTERSECT",VERTEX,{"derivedFrom":[subQ1,subQ0]});Q209=makeQuery(id+"F0.imprint","IMPRINT",FACE,{"disambiguationData":[TD([[makeQuery(id+"F0.imprint","IMPRINT",EDGE,{"disambiguationData":[TD([[subQ2,-1.0]])],"derivedFrom":subQ1}),1.0]])]});}
            var Q210;
            {var subQ0=sQuery(id+"F0.wireOp",EDGE,"E8");var subQ1=sQuery(id+"F0.wireOp",EDGE,"E0.top");var subQ2=makeQuery(id+"F0.imprint","INTERSECT",VERTEX,{"derivedFrom":[subQ1,subQ0]});Q210=makeQuery(id+"F0.imprint","IMPRINT",FACE,{"disambiguationData":[TD([[makeQuery(id+"F0.imprint","IMPRINT",EDGE,{"disambiguationData":[TD([[subQ2,-1.0]])],"derivedFrom":subQ1}),1.0]])]});}
            var Q211;
            {var subQ0=sQuery(id+"F0.wireOp",EDGE,"E34");var subQ1=sQuery(id+"F0.wireOp",EDGE,"E8");var subQ2=makeQuery(id+"F0.imprint","INTERSECT",VERTEX,{"derivedFrom":[subQ1,subQ0]});Q211=makeQuery(id+"F0.imprint","IMPRINT",FACE,{"disambiguationData":[TD([[makeQuery(id+"F0.imprint","IMPRINT",EDGE,{"disambiguationData":[TD([[subQ2,-1.0]])],"derivedFrom":subQ1}),1.0]])]});}
            var Q212;
            {var subQ0=sQuery(id+"F0.wireOp",EDGE,"E29");var subQ1=sQuery(id+"F0.wireOp",EDGE,"E0.right");var subQ2=makeQuery(id+"F0.imprint","INTERSECT",VERTEX,{"derivedFrom":[subQ1,subQ0]});Q212=makeQuery(id+"F0.imprint","IMPRINT",FACE,{"disambiguationData":[TD([[makeQuery(id+"F0.imprint","IMPRINT",EDGE,{"disambiguationData":[TD([[subQ2,-1.0]])],"derivedFrom":subQ1}),-1.0]])]});}
            var Q213;
            {var subQ0=sQuery(id+"F0.wireOp",EDGE,"E28");var subQ1=sQuery(id+"F0.wireOp",EDGE,"E17");var subQ2=makeQuery(id+"F0.imprint","INTERSECT",VERTEX,{"derivedFrom":[subQ1,subQ0]});Q213=makeQuery(id+"F0.imprint","IMPRINT",FACE,{"disambiguationData":[TD([[makeQuery(id+"F0.imprint","IMPRINT",EDGE,{"disambiguationData":[TD([[subQ2,-1.0]])],"derivedFrom":subQ1}),1.0]])]});}
            var Q214;
            {var subQ0=sQuery(id+"F0.wireOp",EDGE,"E34");var subQ1=sQuery(id+"F0.wireOp",EDGE,"E2");var subQ2=makeQuery(id+"F0.imprint","INTERSECT",VERTEX,{"derivedFrom":[subQ1,subQ0]});Q214=makeQuery(id+"F0.imprint","IMPRINT",FACE,{"disambiguationData":[TD([[makeQuery(id+"F0.imprint","IMPRINT",EDGE,{"disambiguationData":[TD([[subQ2,-1.0]])],"derivedFrom":subQ1}),1.0]])]});}
            var Q215;
            {var subQ0=sQuery(id+"F0.wireOp",EDGE,"E15");var subQ1=sQuery(id+"F0.wireOp",EDGE,"E0.bottom");var subQ2=makeQuery(id+"F0.imprint","INTERSECT",VERTEX,{"derivedFrom":[subQ1,subQ0]});Q215=makeQuery(id+"F0.imprint","IMPRINT",FACE,{"disambiguationData":[TD([[makeQuery(id+"F0.imprint","IMPRINT",EDGE,{"disambiguationData":[TD([[subQ2,-1.0]])],"derivedFrom":subQ1}),-1.0]])]});}
            var Q216;
            {var subQ0=sQuery(id+"F0.wireOp",EDGE,"E28");var subQ1=sQuery(id+"F0.wireOp",EDGE,"E9");var subQ2=makeQuery(id+"F0.imprint","INTERSECT",VERTEX,{"derivedFrom":[subQ1,subQ0]});Q216=makeQuery(id+"F0.imprint","IMPRINT",FACE,{"disambiguationData":[TD([[makeQuery(id+"F0.imprint","IMPRINT",EDGE,{"disambiguationData":[TD([[subQ2,-1.0]])],"derivedFrom":subQ1}),1.0]])]});}
            var Q217;
            {var subQ0=sQuery(id+"F0.wireOp",EDGE,"E5");var subQ1=sQuery(id+"F0.wireOp",EDGE,"E0.bottom");var subQ2=makeQuery(id+"F0.imprint","INTERSECT",VERTEX,{"derivedFrom":[subQ1,subQ0]});Q217=makeQuery(id+"F0.imprint","IMPRINT",FACE,{"disambiguationData":[TD([[makeQuery(id+"F0.imprint","IMPRINT",EDGE,{"disambiguationData":[TD([[subQ2,-1.0]])],"derivedFrom":subQ1}),-1.0]])]});}
            var Q218;
            {var subQ0=sQuery(id+"F0.wireOp",EDGE,"E2");var subQ1=sQuery(id+"F0.wireOp",EDGE,"E0.bottom");var subQ2=makeQuery(id+"F0.imprint","INTERSECT",VERTEX,{"derivedFrom":[subQ1,subQ0]});Q218=makeQuery(id+"F0.imprint","IMPRINT",FACE,{"disambiguationData":[TD([[makeQuery(id+"F0.imprint","IMPRINT",EDGE,{"disambiguationData":[TD([[subQ2,-1.0]])],"derivedFrom":subQ1}),-1.0]])]});}
            var Q219;
            {var subQ0=sQuery(id+"F0.wireOp",EDGE,"E34");var subQ1=sQuery(id+"F0.wireOp",EDGE,"E14");var subQ2=makeQuery(id+"F0.imprint","INTERSECT",VERTEX,{"derivedFrom":[subQ1,subQ0]});Q219=makeQuery(id+"F0.imprint","IMPRINT",FACE,{"disambiguationData":[TD([[makeQuery(id+"F0.imprint","IMPRINT",EDGE,{"disambiguationData":[TD([[subQ2,-1.0]])],"derivedFrom":subQ1}),1.0]])]});}
            var Q220;
            {var subQ0=sQuery(id+"F0.wireOp",EDGE,"E3");var subQ1=sQuery(id+"F0.wireOp",EDGE,"E0.bottom");var subQ2=makeQuery(id+"F0.imprint","INTERSECT",VERTEX,{"derivedFrom":[subQ1,subQ0]});Q220=makeQuery(id+"F0.imprint","IMPRINT",FACE,{"disambiguationData":[TD([[makeQuery(id+"F0.imprint","IMPRINT",EDGE,{"disambiguationData":[TD([[subQ2,-1.0]])],"derivedFrom":subQ1}),-1.0]])]});}
            var Q221;
            {var subQ0=sQuery(id+"F0.wireOp",EDGE,"E28");var subQ1=sQuery(id+"F0.wireOp",EDGE,"E7");var subQ2=makeQuery(id+"F0.imprint","INTERSECT",VERTEX,{"derivedFrom":[subQ1,subQ0]});Q221=makeQuery(id+"F0.imprint","IMPRINT",FACE,{"disambiguationData":[TD([[makeQuery(id+"F0.imprint","IMPRINT",EDGE,{"disambiguationData":[TD([[subQ2,-1.0]])],"derivedFrom":subQ1}),1.0]])]});}
            var Q222;
            {var subQ0=sQuery(id+"F0.wireOp",EDGE,"E34");var subQ1=sQuery(id+"F0.wireOp",EDGE,"E9");var subQ2=makeQuery(id+"F0.imprint","INTERSECT",VERTEX,{"derivedFrom":[subQ1,subQ0]});Q222=makeQuery(id+"F0.imprint","IMPRINT",FACE,{"disambiguationData":[TD([[makeQuery(id+"F0.imprint","IMPRINT",EDGE,{"disambiguationData":[TD([[subQ2,-1.0]])],"derivedFrom":subQ1}),1.0]])]});}
            var Q223;
            {var subQ0=sQuery(id+"F0.wireOp",EDGE,"E13");var subQ1=sQuery(id+"F0.wireOp",EDGE,"E0.top");var subQ2=makeQuery(id+"F0.imprint","INTERSECT",VERTEX,{"derivedFrom":[subQ1,subQ0]});Q223=makeQuery(id+"F0.imprint","IMPRINT",FACE,{"disambiguationData":[TD([[makeQuery(id+"F0.imprint","IMPRINT",EDGE,{"disambiguationData":[TD([[subQ2,-1.0]])],"derivedFrom":subQ1}),1.0]])]});}
            var Q224;
            {var subQ0=sQuery(id+"F0.wireOp",EDGE,"E28");var subQ1=sQuery(id+"F0.wireOp",EDGE,"E0.left");var subQ2=makeQuery(id+"F0.imprint","INTERSECT",VERTEX,{"derivedFrom":[subQ1,subQ0]});Q224=makeQuery(id+"F0.imprint","IMPRINT",FACE,{"disambiguationData":[TD([[makeQuery(id+"F0.imprint","IMPRINT",EDGE,{"disambiguationData":[TD([[subQ2,-1.0]])],"derivedFrom":subQ1}),1.0]])]});}
            var Q225;
            {var subQ0=sQuery(id+"F0.wireOp",EDGE,"E29");var subQ1=sQuery(id+"F0.wireOp",EDGE,"E4");var subQ2=makeQuery(id+"F0.imprint","INTERSECT",VERTEX,{"derivedFrom":[subQ1,subQ0]});Q225=makeQuery(id+"F0.imprint","IMPRINT",FACE,{"disambiguationData":[TD([[makeQuery(id+"F0.imprint","IMPRINT",EDGE,{"disambiguationData":[TD([[subQ2,-1.0]])],"derivedFrom":subQ1}),1.0]])]});}
            var Q226;
            {var subQ0=sQuery(id+"F0.wireOp",EDGE,"E20");var subQ1=sQuery(id+"F0.wireOp",EDGE,"E2");var subQ2=makeQuery(id+"F0.imprint","INTERSECT",VERTEX,{"derivedFrom":[subQ1,subQ0]});Q226=makeQuery(id+"F0.imprint","IMPRINT",FACE,{"disambiguationData":[TD([[makeQuery(id+"F0.imprint","IMPRINT",EDGE,{"disambiguationData":[TD([[subQ2,-1.0]])],"derivedFrom":subQ1}),1.0]])]});}
            var Q227;
            {var subQ0=sQuery(id+"F0.wireOp",EDGE,"E27");var subQ1=sQuery(id+"F0.wireOp",EDGE,"E4");var subQ2=makeQuery(id+"F0.imprint","INTERSECT",VERTEX,{"derivedFrom":[subQ1,subQ0]});Q227=makeQuery(id+"F0.imprint","IMPRINT",FACE,{"disambiguationData":[TD([[makeQuery(id+"F0.imprint","IMPRINT",EDGE,{"disambiguationData":[TD([[subQ2,-1.0]])],"derivedFrom":subQ1}),1.0]])]});}
            var Q228;
            {var subQ0=sQuery(id+"F0.wireOp",EDGE,"E10");var subQ1=sQuery(id+"F0.wireOp",EDGE,"E0.top");var subQ2=makeQuery(id+"F0.imprint","INTERSECT",VERTEX,{"derivedFrom":[subQ1,subQ0]});Q228=makeQuery(id+"F0.imprint","IMPRINT",FACE,{"disambiguationData":[TD([[makeQuery(id+"F0.imprint","IMPRINT",EDGE,{"disambiguationData":[TD([[subQ2,-1.0]])],"derivedFrom":subQ1}),1.0]])]});}
            var Q229;
            {var subQ0=sQuery(id+"F0.wireOp",EDGE,"E21");var subQ1=sQuery(id+"F0.wireOp",EDGE,"E0.left");var subQ2=makeQuery(id+"F0.imprint","INTERSECT",VERTEX,{"derivedFrom":[subQ1,subQ0]});Q229=makeQuery(id+"F0.imprint","IMPRINT",FACE,{"disambiguationData":[TD([[makeQuery(id+"F0.imprint","IMPRINT",EDGE,{"disambiguationData":[TD([[subQ2,-1.0]])],"derivedFrom":subQ1}),1.0]])]});}
            var Q230;
            {var subQ0=sQuery(id+"F0.wireOp",EDGE,"E28");var subQ1=sQuery(id+"F0.wireOp",EDGE,"E15");var subQ2=makeQuery(id+"F0.imprint","INTERSECT",VERTEX,{"derivedFrom":[subQ1,subQ0]});Q230=makeQuery(id+"F0.imprint","IMPRINT",FACE,{"disambiguationData":[TD([[makeQuery(id+"F0.imprint","IMPRINT",EDGE,{"disambiguationData":[TD([[subQ2,-1.0]])],"derivedFrom":subQ1}),1.0]])]});}
            var Q231;
            {var subQ0=sQuery(id+"F0.wireOp",EDGE,"E9");var subQ1=sQuery(id+"F0.wireOp",EDGE,"E0.top");var subQ2=makeQuery(id+"F0.imprint","INTERSECT",VERTEX,{"derivedFrom":[subQ1,subQ0]});Q231=makeQuery(id+"F0.imprint","IMPRINT",FACE,{"disambiguationData":[TD([[makeQuery(id+"F0.imprint","IMPRINT",EDGE,{"disambiguationData":[TD([[subQ2,-1.0]])],"derivedFrom":subQ1}),1.0]])]});}
            var Q232;
            {var subQ0=sQuery(id+"F0.wireOp",EDGE,"E34");var subQ1=sQuery(id+"F0.wireOp",EDGE,"E13");var subQ2=makeQuery(id+"F0.imprint","INTERSECT",VERTEX,{"derivedFrom":[subQ1,subQ0]});Q232=makeQuery(id+"F0.imprint","IMPRINT",FACE,{"disambiguationData":[TD([[makeQuery(id+"F0.imprint","IMPRINT",EDGE,{"disambiguationData":[TD([[subQ2,-1.0]])],"derivedFrom":subQ1}),1.0]])]});}
            var Q233;
            {var subQ0=sQuery(id+"F0.wireOp",EDGE,"E29");var subQ1=sQuery(id+"F0.wireOp",EDGE,"E0.left");var subQ2=makeQuery(id+"F0.imprint","INTERSECT",VERTEX,{"derivedFrom":[subQ1,subQ0]});Q233=makeQuery(id+"F0.imprint","IMPRINT",FACE,{"disambiguationData":[TD([[makeQuery(id+"F0.imprint","IMPRINT",EDGE,{"disambiguationData":[TD([[subQ2,-1.0]])],"derivedFrom":subQ1}),1.0]])]});}
            var Q234;
            {var subQ0=sQuery(id+"F0.wireOp",EDGE,"E31");var subQ1=sQuery(id+"F0.wireOp",EDGE,"E0.right");var subQ2=makeQuery(id+"F0.imprint","INTERSECT",VERTEX,{"derivedFrom":[subQ1,subQ0]});Q234=makeQuery(id+"F0.imprint","IMPRINT",FACE,{"disambiguationData":[TD([[makeQuery(id+"F0.imprint","IMPRINT",EDGE,{"disambiguationData":[TD([[subQ2,-1.0]])],"derivedFrom":subQ1}),-1.0]])]});}
            var Q235;
            {var subQ0=sQuery(id+"F0.wireOp",EDGE,"E11");var subQ1=sQuery(id+"F0.wireOp",EDGE,"E0.top");var subQ2=makeQuery(id+"F0.imprint","INTERSECT",VERTEX,{"derivedFrom":[subQ1,subQ0]});Q235=makeQuery(id+"F0.imprint","IMPRINT",FACE,{"disambiguationData":[TD([[makeQuery(id+"F0.imprint","IMPRINT",EDGE,{"disambiguationData":[TD([[subQ2,-1.0]])],"derivedFrom":subQ1}),1.0]])]});}
            var Q236;
            {var subQ0=sQuery(id+"F0.wireOp",EDGE,"E4");var subQ1=sQuery(id+"F0.wireOp",EDGE,"E0.top");var subQ2=makeQuery(id+"F0.imprint","INTERSECT",VERTEX,{"derivedFrom":[subQ1,subQ0]});Q236=makeQuery(id+"F0.imprint","IMPRINT",FACE,{"disambiguationData":[TD([[makeQuery(id+"F0.imprint","IMPRINT",EDGE,{"disambiguationData":[TD([[subQ2,-1.0]])],"derivedFrom":subQ1}),1.0]])]});}
            var Q237;
            {var subQ0=sQuery(id+"F0.wireOp",EDGE,"E12");var subQ1=sQuery(id+"F0.wireOp",EDGE,"E0.top");var subQ2=makeQuery(id+"F0.imprint","INTERSECT",VERTEX,{"derivedFrom":[subQ1,subQ0]});Q237=makeQuery(id+"F0.imprint","IMPRINT",FACE,{"disambiguationData":[TD([[makeQuery(id+"F0.imprint","IMPRINT",EDGE,{"disambiguationData":[TD([[subQ2,-1.0]])],"derivedFrom":subQ1}),1.0]])]});}
            var Q238;
            {var subQ0=sQuery(id+"F0.wireOp",EDGE,"E28");var subQ1=sQuery(id+"F0.wireOp",EDGE,"E8");var subQ2=makeQuery(id+"F0.imprint","INTERSECT",VERTEX,{"derivedFrom":[subQ1,subQ0]});Q238=makeQuery(id+"F0.imprint","IMPRINT",FACE,{"disambiguationData":[TD([[makeQuery(id+"F0.imprint","IMPRINT",EDGE,{"disambiguationData":[TD([[subQ2,-1.0]])],"derivedFrom":subQ1}),1.0]])]});}
            var Q239;
            {var subQ0=sQuery(id+"F0.wireOp",EDGE,"E20");var subQ1=sQuery(id+"F0.wireOp",EDGE,"E7");var subQ2=makeQuery(id+"F0.imprint","INTERSECT",VERTEX,{"derivedFrom":[subQ1,subQ0]});Q239=makeQuery(id+"F0.imprint","IMPRINT",FACE,{"disambiguationData":[TD([[makeQuery(id+"F0.imprint","IMPRINT",EDGE,{"disambiguationData":[TD([[subQ2,-1.0]])],"derivedFrom":subQ1}),1.0]])]});}
            var Q240;
            {var subQ0=sQuery(id+"F0.wireOp",EDGE,"E2");var subQ1=sQuery(id+"F0.wireOp",EDGE,"E0.top");var subQ2=makeQuery(id+"F0.imprint","INTERSECT",VERTEX,{"derivedFrom":[subQ1,subQ0]});Q240=makeQuery(id+"F0.imprint","IMPRINT",FACE,{"disambiguationData":[TD([[makeQuery(id+"F0.imprint","IMPRINT",EDGE,{"disambiguationData":[TD([[subQ2,-1.0]])],"derivedFrom":subQ1}),1.0]])]});}
            var Q241;
            {var subQ0=sQuery(id+"F0.wireOp",EDGE,"E28");var subQ1=sQuery(id+"F0.wireOp",EDGE,"E2");var subQ2=makeQuery(id+"F0.imprint","INTERSECT",VERTEX,{"derivedFrom":[subQ1,subQ0]});Q241=makeQuery(id+"F0.imprint","IMPRINT",FACE,{"disambiguationData":[TD([[makeQuery(id+"F0.imprint","IMPRINT",EDGE,{"disambiguationData":[TD([[subQ2,-1.0]])],"derivedFrom":subQ1}),1.0]])]});}
            var Q242;
            {var subQ0=sQuery(id+"F0.wireOp",EDGE,"E28");var subQ1=sQuery(id+"F0.wireOp",EDGE,"E5");var subQ2=makeQuery(id+"F0.imprint","INTERSECT",VERTEX,{"derivedFrom":[subQ1,subQ0]});Q242=makeQuery(id+"F0.imprint","IMPRINT",FACE,{"disambiguationData":[TD([[makeQuery(id+"F0.imprint","IMPRINT",EDGE,{"disambiguationData":[TD([[subQ2,-1.0]])],"derivedFrom":subQ1}),1.0]])]});}
            var Q243;
            {var subQ0=sQuery(id+"F0.wireOp",EDGE,"E34");var subQ1=sQuery(id+"F0.wireOp",EDGE,"E6");var subQ2=makeQuery(id+"F0.imprint","INTERSECT",VERTEX,{"derivedFrom":[subQ1,subQ0]});Q243=makeQuery(id+"F0.imprint","IMPRINT",FACE,{"disambiguationData":[TD([[makeQuery(id+"F0.imprint","IMPRINT",EDGE,{"disambiguationData":[TD([[subQ2,-1.0]])],"derivedFrom":subQ1}),1.0]])]});}
            var Q244;
            {var subQ0=sQuery(id+"F0.wireOp",EDGE,"E17");var subQ1=sQuery(id+"F0.wireOp",EDGE,"E0.top");var subQ2=makeQuery(id+"F0.imprint","INTERSECT",VERTEX,{"derivedFrom":[subQ1,subQ0]});Q244=makeQuery(id+"F0.imprint","IMPRINT",FACE,{"disambiguationData":[TD([[makeQuery(id+"F0.imprint","IMPRINT",EDGE,{"disambiguationData":[TD([[subQ2,-1.0]])],"derivedFrom":subQ1}),1.0]])]});}
            var Q245;
            {var subQ0=sQuery(id+"F0.wireOp",EDGE,"E21");var subQ1=sQuery(id+"F0.wireOp",EDGE,"E4");var subQ2=makeQuery(id+"F0.imprint","INTERSECT",VERTEX,{"derivedFrom":[subQ1,subQ0]});Q245=makeQuery(id+"F0.imprint","IMPRINT",FACE,{"disambiguationData":[TD([[makeQuery(id+"F0.imprint","IMPRINT",EDGE,{"disambiguationData":[TD([[subQ2,-1.0]])],"derivedFrom":subQ1}),1.0]])]});}
            var Q246;
            {var subQ0=sQuery(id+"F0.wireOp",EDGE,"E19");var subQ1=sQuery(id+"F0.wireOp",EDGE,"E0.right");var subQ2=makeQuery(id+"F0.imprint","INTERSECT",VERTEX,{"derivedFrom":[subQ1,subQ0]});Q246=makeQuery(id+"F0.imprint","IMPRINT",FACE,{"disambiguationData":[TD([[makeQuery(id+"F0.imprint","IMPRINT",EDGE,{"disambiguationData":[TD([[subQ2,-1.0]])],"derivedFrom":subQ1}),-1.0]])]});}
            var Q247;
            {var subQ0=sQuery(id+"F0.wireOp",EDGE,"E5");var subQ1=sQuery(id+"F0.wireOp",EDGE,"E0.top");var subQ2=makeQuery(id+"F0.imprint","INTERSECT",VERTEX,{"derivedFrom":[subQ1,subQ0]});Q247=makeQuery(id+"F0.imprint","IMPRINT",FACE,{"disambiguationData":[TD([[makeQuery(id+"F0.imprint","IMPRINT",EDGE,{"disambiguationData":[TD([[subQ2,-1.0]])],"derivedFrom":subQ1}),1.0]])]});}
            var Q248;
            {var subQ0=sQuery(id+"F0.wireOp",EDGE,"E26");var subQ1=sQuery(id+"F0.wireOp",EDGE,"E4");var subQ2=makeQuery(id+"F0.imprint","INTERSECT",VERTEX,{"derivedFrom":[subQ1,subQ0]});Q248=makeQuery(id+"F0.imprint","IMPRINT",FACE,{"disambiguationData":[TD([[makeQuery(id+"F0.imprint","IMPRINT",EDGE,{"disambiguationData":[TD([[subQ2,-1.0]])],"derivedFrom":subQ1}),1.0]])]});}
            var Q249;
            {var subQ0=sQuery(id+"F0.wireOp",EDGE,"E1");var subQ1=sQuery(id+"F0.wireOp",EDGE,"E0.bottom");var subQ2=makeQuery(id+"F0.imprint","INTERSECT",VERTEX,{"derivedFrom":[subQ1,subQ0]});Q249=makeQuery(id+"F0.imprint","IMPRINT",FACE,{"disambiguationData":[TD([[makeQuery(id+"F0.imprint","IMPRINT",EDGE,{"disambiguationData":[TD([[subQ2,-1.0]])],"derivedFrom":subQ1}),-1.0]])]});}
            var Q250;
            {var subQ0=sQuery(id+"F0.wireOp",EDGE,"E33");var subQ1=sQuery(id+"F0.wireOp",EDGE,"E4");var subQ2=makeQuery(id+"F0.imprint","INTERSECT",VERTEX,{"derivedFrom":[subQ1,subQ0]});Q250=makeQuery(id+"F0.imprint","IMPRINT",FACE,{"disambiguationData":[TD([[makeQuery(id+"F0.imprint","IMPRINT",EDGE,{"disambiguationData":[TD([[subQ2,-1.0]])],"derivedFrom":subQ1}),1.0]])]});}
            var Q251;
            {var subQ0=sQuery(id+"F0.wireOp",EDGE,"E19");var subQ1=sQuery(id+"F0.wireOp",EDGE,"E4");var subQ2=makeQuery(id+"F0.imprint","INTERSECT",VERTEX,{"derivedFrom":[subQ1,subQ0]});Q251=makeQuery(id+"F0.imprint","IMPRINT",FACE,{"disambiguationData":[TD([[makeQuery(id+"F0.imprint","IMPRINT",EDGE,{"disambiguationData":[TD([[subQ2,-1.0]])],"derivedFrom":subQ1}),1.0]])]});}
            var Q252;
            {var subQ0=sQuery(id+"F0.wireOp",EDGE,"E3");var subQ1=sQuery(id+"F0.wireOp",EDGE,"E0.top");var subQ2=makeQuery(id+"F0.imprint","INTERSECT",VERTEX,{"derivedFrom":[subQ1,subQ0]});Q252=makeQuery(id+"F0.imprint","IMPRINT",FACE,{"disambiguationData":[TD([[makeQuery(id+"F0.imprint","IMPRINT",EDGE,{"disambiguationData":[TD([[subQ2,-1.0]])],"derivedFrom":subQ1}),1.0]])]});}
            var Q253;
            {var subQ0=sQuery(id+"F0.wireOp",EDGE,"E28");var subQ1=sQuery(id+"F0.wireOp",EDGE,"E0.right");var subQ2=makeQuery(id+"F0.imprint","INTERSECT",VERTEX,{"derivedFrom":[subQ1,subQ0]});Q253=makeQuery(id+"F0.imprint","IMPRINT",FACE,{"disambiguationData":[TD([[makeQuery(id+"F0.imprint","IMPRINT",EDGE,{"disambiguationData":[TD([[subQ2,-1.0]])],"derivedFrom":subQ1}),-1.0]])]});}
            var Q254;
            {var subQ0=sQuery(id+"F0.wireOp",EDGE,"E23");var subQ1=sQuery(id+"F0.wireOp",EDGE,"E4");var subQ2=makeQuery(id+"F0.imprint","INTERSECT",VERTEX,{"derivedFrom":[subQ1,subQ0]});Q254=makeQuery(id+"F0.imprint","IMPRINT",FACE,{"disambiguationData":[TD([[makeQuery(id+"F0.imprint","IMPRINT",EDGE,{"disambiguationData":[TD([[subQ2,-1.0]])],"derivedFrom":subQ1}),1.0]])]});}
            var Q255;
            {var subQ0=sQuery(id+"F0.wireOp",EDGE,"E32");var subQ1=sQuery(id+"F0.wireOp",EDGE,"E0.right");var subQ2=makeQuery(id+"F0.imprint","INTERSECT",VERTEX,{"derivedFrom":[subQ1,subQ0]});Q255=makeQuery(id+"F0.imprint","IMPRINT",FACE,{"disambiguationData":[TD([[makeQuery(id+"F0.imprint","IMPRINT",EDGE,{"disambiguationData":[TD([[subQ2,-1.0]])],"derivedFrom":subQ1}),-1.0]])]});}
            var Q256;
            {var subQ0=sQuery(id+"F0.wireOp",EDGE,"E27");var subQ1=sQuery(id+"F0.wireOp",EDGE,"E0.right");var subQ2=makeQuery(id+"F0.imprint","INTERSECT",VERTEX,{"derivedFrom":[subQ1,subQ0]});Q256=makeQuery(id+"F0.imprint","IMPRINT",FACE,{"disambiguationData":[TD([[makeQuery(id+"F0.imprint","IMPRINT",EDGE,{"disambiguationData":[TD([[subQ2,-1.0]])],"derivedFrom":subQ1}),-1.0]])]});}
            var Q257;
            {var subQ0=sQuery(id+"F0.wireOp",EDGE,"E6");var subQ1=sQuery(id+"F0.wireOp",EDGE,"E0.top");var subQ2=makeQuery(id+"F0.imprint","INTERSECT",VERTEX,{"derivedFrom":[subQ1,subQ0]});Q257=makeQuery(id+"F0.imprint","IMPRINT",FACE,{"disambiguationData":[TD([[makeQuery(id+"F0.imprint","IMPRINT",EDGE,{"disambiguationData":[TD([[subQ2,-1.0]])],"derivedFrom":subQ1}),1.0]])]});}
            var Q258;
            {var subQ0=sQuery(id+"F0.wireOp",EDGE,"E20");var subQ1=sQuery(id+"F0.wireOp",EDGE,"E0.left");var subQ2=makeQuery(id+"F0.imprint","INTERSECT",VERTEX,{"derivedFrom":[subQ1,subQ0]});Q258=makeQuery(id+"F0.imprint","IMPRINT",FACE,{"disambiguationData":[TD([[makeQuery(id+"F0.imprint","IMPRINT",EDGE,{"disambiguationData":[TD([[subQ2,-1.0]])],"derivedFrom":subQ1}),1.0]])]});}
            var Q259;
            {var subQ0=sQuery(id+"F0.wireOp",EDGE,"E27");var subQ1=sQuery(id+"F0.wireOp",EDGE,"E0.left");var subQ2=makeQuery(id+"F0.imprint","INTERSECT",VERTEX,{"derivedFrom":[subQ1,subQ0]});Q259=makeQuery(id+"F0.imprint","IMPRINT",FACE,{"disambiguationData":[TD([[makeQuery(id+"F0.imprint","IMPRINT",EDGE,{"disambiguationData":[TD([[subQ2,-1.0]])],"derivedFrom":subQ1}),1.0]])]});}
            var Q260;
            {var subQ0=sQuery(id+"F0.wireOp",EDGE,"E34");var subQ1=sQuery(id+"F0.wireOp",EDGE,"E5");var subQ2=makeQuery(id+"F0.imprint","INTERSECT",VERTEX,{"derivedFrom":[subQ1,subQ0]});Q260=makeQuery(id+"F0.imprint","IMPRINT",FACE,{"disambiguationData":[TD([[makeQuery(id+"F0.imprint","IMPRINT",EDGE,{"disambiguationData":[TD([[subQ2,-1.0]])],"derivedFrom":subQ1}),1.0]])]});}
            var Q261;
            {var subQ0=sQuery(id+"F0.wireOp",EDGE,"E9");var subQ1=sQuery(id+"F0.wireOp",EDGE,"E0.bottom");var subQ2=makeQuery(id+"F0.imprint","INTERSECT",VERTEX,{"derivedFrom":[subQ1,subQ0]});Q261=makeQuery(id+"F0.imprint","IMPRINT",FACE,{"disambiguationData":[TD([[makeQuery(id+"F0.imprint","IMPRINT",EDGE,{"disambiguationData":[TD([[subQ2,-1.0]])],"derivedFrom":subQ1}),-1.0]])]});}
            var Q262;
            {var subQ0=sQuery(id+"F0.wireOp",EDGE,"E28");var subQ1=sQuery(id+"F0.wireOp",EDGE,"E14");var subQ2=makeQuery(id+"F0.imprint","INTERSECT",VERTEX,{"derivedFrom":[subQ1,subQ0]});Q262=makeQuery(id+"F0.imprint","IMPRINT",FACE,{"disambiguationData":[TD([[makeQuery(id+"F0.imprint","IMPRINT",EDGE,{"disambiguationData":[TD([[subQ2,-1.0]])],"derivedFrom":subQ1}),1.0]])]});}
            var Q263;
            {var subQ0=sQuery(id+"F0.wireOp",EDGE,"E34");var subQ1=sQuery(id+"F0.wireOp",EDGE,"E0.right");var subQ2=makeQuery(id+"F0.imprint","INTERSECT",VERTEX,{"derivedFrom":[subQ1,subQ0]});Q263=makeQuery(id+"F0.imprint","IMPRINT",FACE,{"disambiguationData":[TD([[makeQuery(id+"F0.imprint","IMPRINT",EDGE,{"disambiguationData":[TD([[subQ2,-1.0]])],"derivedFrom":subQ1}),-1.0]])]});}
            var Q264;
            {var subQ0=sQuery(id+"F0.wireOp",EDGE,"E28");var subQ1=sQuery(id+"F0.wireOp",EDGE,"E16");var subQ2=makeQuery(id+"F0.imprint","INTERSECT",VERTEX,{"derivedFrom":[subQ1,subQ0]});Q264=makeQuery(id+"F0.imprint","IMPRINT",FACE,{"disambiguationData":[TD([[makeQuery(id+"F0.imprint","IMPRINT",EDGE,{"disambiguationData":[TD([[subQ2,-1.0]])],"derivedFrom":subQ1}),1.0]])]});}
            var Q265;
            {var subQ0=sQuery(id+"F0.wireOp",EDGE,"E24");var subQ1=sQuery(id+"F0.wireOp",EDGE,"E0.right");var subQ2=makeQuery(id+"F0.imprint","INTERSECT",VERTEX,{"derivedFrom":[subQ1,subQ0]});Q265=makeQuery(id+"F0.imprint","IMPRINT",FACE,{"disambiguationData":[TD([[makeQuery(id+"F0.imprint","IMPRINT",EDGE,{"disambiguationData":[TD([[subQ2,-1.0]])],"derivedFrom":subQ1}),-1.0]])]});}
            var Q266;
            {var subQ0=sQuery(id+"F0.wireOp",EDGE,"E20");var subQ1=sQuery(id+"F0.wireOp",EDGE,"E13");var subQ2=makeQuery(id+"F0.imprint","INTERSECT",VERTEX,{"derivedFrom":[subQ1,subQ0]});Q266=makeQuery(id+"F0.imprint","IMPRINT",FACE,{"disambiguationData":[TD([[makeQuery(id+"F0.imprint","IMPRINT",EDGE,{"disambiguationData":[TD([[subQ2,-1.0]])],"derivedFrom":subQ1}),1.0]])]});}
            var Q267;
            {var subQ0=sQuery(id+"F0.wireOp",EDGE,"E20");var subQ1=sQuery(id+"F0.wireOp",EDGE,"E12");var subQ2=makeQuery(id+"F0.imprint","INTERSECT",VERTEX,{"derivedFrom":[subQ1,subQ0]});Q267=makeQuery(id+"F0.imprint","IMPRINT",FACE,{"disambiguationData":[TD([[makeQuery(id+"F0.imprint","IMPRINT",EDGE,{"disambiguationData":[TD([[subQ2,-1.0]])],"derivedFrom":subQ1}),1.0]])]});}
            var Q268;
            {var subQ0=sQuery(id+"F0.wireOp",EDGE,"E12");var subQ1=sQuery(id+"F0.wireOp",EDGE,"E0.bottom");var subQ2=makeQuery(id+"F0.imprint","INTERSECT",VERTEX,{"derivedFrom":[subQ1,subQ0]});Q268=makeQuery(id+"F0.imprint","IMPRINT",FACE,{"disambiguationData":[TD([[makeQuery(id+"F0.imprint","IMPRINT",EDGE,{"disambiguationData":[TD([[subQ2,-1.0]])],"derivedFrom":subQ1}),-1.0]])]});}
            var Q269;
            {var subQ0=sQuery(id+"F0.wireOp",EDGE,"E6");var subQ1=sQuery(id+"F0.wireOp",EDGE,"E0.bottom");var subQ2=makeQuery(id+"F0.imprint","INTERSECT",VERTEX,{"derivedFrom":[subQ1,subQ0]});Q269=makeQuery(id+"F0.imprint","IMPRINT",FACE,{"disambiguationData":[TD([[makeQuery(id+"F0.imprint","IMPRINT",EDGE,{"disambiguationData":[TD([[subQ2,-1.0]])],"derivedFrom":subQ1}),-1.0]])]});}
            var Q270;
            {var subQ0=sQuery(id+"F0.wireOp",EDGE,"E10");var subQ1=sQuery(id+"F0.wireOp",EDGE,"E0.bottom");var subQ2=makeQuery(id+"F0.imprint","INTERSECT",VERTEX,{"derivedFrom":[subQ1,subQ0]});Q270=makeQuery(id+"F0.imprint","IMPRINT",FACE,{"disambiguationData":[TD([[makeQuery(id+"F0.imprint","IMPRINT",EDGE,{"disambiguationData":[TD([[subQ2,-1.0]])],"derivedFrom":subQ1}),-1.0]])]});}
            var Q271;
            {var subQ0=sQuery(id+"F0.wireOp",EDGE,"E34");var subQ1=sQuery(id+"F0.wireOp",EDGE,"E3");var subQ2=makeQuery(id+"F0.imprint","INTERSECT",VERTEX,{"derivedFrom":[subQ1,subQ0]});Q271=makeQuery(id+"F0.imprint","IMPRINT",FACE,{"disambiguationData":[TD([[makeQuery(id+"F0.imprint","IMPRINT",EDGE,{"disambiguationData":[TD([[subQ2,-1.0]])],"derivedFrom":subQ1}),1.0]])]});}
            var Q272;
            {var subQ0=sQuery(id+"F0.wireOp",EDGE,"E15");var subQ1=sQuery(id+"F0.wireOp",EDGE,"E0.top");var subQ2=makeQuery(id+"F0.imprint","INTERSECT",VERTEX,{"derivedFrom":[subQ1,subQ0]});Q272=makeQuery(id+"F0.imprint","IMPRINT",FACE,{"disambiguationData":[TD([[makeQuery(id+"F0.imprint","IMPRINT",EDGE,{"disambiguationData":[TD([[subQ2,-1.0]])],"derivedFrom":subQ1}),1.0]])]});}
            var Q273;
            {var subQ0=sQuery(id+"F0.wireOp",EDGE,"E28");var subQ1=sQuery(id+"F0.wireOp",EDGE,"E4");var subQ2=makeQuery(id+"F0.imprint","INTERSECT",VERTEX,{"derivedFrom":[subQ1,subQ0]});Q273=makeQuery(id+"F0.imprint","IMPRINT",FACE,{"disambiguationData":[TD([[makeQuery(id+"F0.imprint","IMPRINT",EDGE,{"disambiguationData":[TD([[subQ2,-1.0]])],"derivedFrom":subQ1}),1.0]])]});}
            var Q274;
            {var subQ0=sQuery(id+"F0.wireOp",EDGE,"E25");var subQ1=sQuery(id+"F0.wireOp",EDGE,"E0.right");var subQ2=makeQuery(id+"F0.imprint","INTERSECT",VERTEX,{"derivedFrom":[subQ1,subQ0]});Q274=makeQuery(id+"F0.imprint","IMPRINT",FACE,{"disambiguationData":[TD([[makeQuery(id+"F0.imprint","IMPRINT",EDGE,{"disambiguationData":[TD([[subQ2,-1.0]])],"derivedFrom":subQ1}),-1.0]])]});}
            var Q275;
            {var subQ0=sQuery(id+"F0.wireOp",EDGE,"E34");var subQ1=sQuery(id+"F0.wireOp",EDGE,"E4");var subQ2=makeQuery(id+"F0.imprint","INTERSECT",VERTEX,{"derivedFrom":[subQ1,subQ0]});Q275=makeQuery(id+"F0.imprint","IMPRINT",FACE,{"disambiguationData":[TD([[makeQuery(id+"F0.imprint","IMPRINT",EDGE,{"disambiguationData":[TD([[subQ2,-1.0]])],"derivedFrom":subQ1}),1.0]])]});}
            var Q276;
            {var subQ0=sQuery(id+"F0.wireOp",EDGE,"E0.right");var subQ1=sQuery(id+"F0.wireOp",EDGE,"E0.top");var subQ2=makeQuery(id+"F0.imprint","INTERSECT",VERTEX,{"derivedFrom":[subQ1,subQ0]});Q276=makeQuery(id+"F0.imprint","IMPRINT",FACE,{"disambiguationData":[TD([[makeQuery(id+"F0.imprint","IMPRINT",EDGE,{"disambiguationData":[TD([[subQ2,1.0]])],"derivedFrom":subQ1}),1.0]])]});}
            var Q277;
            {var subQ0=sQuery(id+"F0.wireOp",EDGE,"E0.right");var subQ1=sQuery(id+"F0.wireOp",EDGE,"E0.bottom");var subQ2=makeQuery(id+"F0.imprint","INTERSECT",VERTEX,{"derivedFrom":[subQ1,subQ0]});Q277=makeQuery(id+"F0.imprint","IMPRINT",FACE,{"disambiguationData":[TD([[makeQuery(id+"F0.imprint","IMPRINT",EDGE,{"disambiguationData":[TD([[subQ2,1.0]])],"derivedFrom":subQ1}),-1.0]])]});}
            var Q278;
            {var subQ0=sQuery(id+"F0.wireOp",EDGE,"E0.left");var subQ1=sQuery(id+"F0.wireOp",EDGE,"E0.top");var subQ2=makeQuery(id+"F0.imprint","INTERSECT",VERTEX,{"derivedFrom":[subQ1,subQ0]});Q278=makeQuery(id+"F0.imprint","IMPRINT",FACE,{"disambiguationData":[TD([[makeQuery(id+"F0.imprint","IMPRINT",EDGE,{"disambiguationData":[TD([[subQ2,-1.0]])],"derivedFrom":subQ1}),1.0]])]});}
            var Q279;
            {var subQ0=sQuery(id+"F0.wireOp",EDGE,"E0.left");var subQ1=sQuery(id+"F0.wireOp",EDGE,"E0.bottom");var subQ2=makeQuery(id+"F0.imprint","INTERSECT",VERTEX,{"derivedFrom":[subQ1,subQ0]});Q279=makeQuery(id+"F0.imprint","IMPRINT",FACE,{"disambiguationData":[TD([[makeQuery(id+"F0.imprint","IMPRINT",EDGE,{"disambiguationData":[TD([[subQ2,-1.0]])],"derivedFrom":subQ1}),-1.0]])]});}
            extrude(context, id + "F1", {"entities" : qUnion([Q0, Q1, Q2, Q3, Q4, Q5, Q6, Q7, Q8, Q9, Q10, Q11, Q12, Q13, Q14, Q15, Q16, Q17, Q18, Q19, Q20, Q21, Q22, Q23, Q24, Q25, Q26, Q27, Q28, Q29, Q30, Q31, Q32, Q33, Q34, Q35, Q36, Q37, Q38, Q39, Q40, Q41, Q42, Q43, Q44, Q45, Q46, Q47, Q48, Q49, Q50, Q51, Q52, Q53, Q54, Q55, Q56, Q57, Q58, Q59, Q60, Q61, Q62, Q63, Q64, Q65, Q66, Q67, Q68, Q69, Q70, Q71, Q72, Q73, Q74, Q75, Q76, Q77, Q78, Q79, Q80, Q81, Q82, Q83, Q84, Q85, Q86, Q87, Q88, Q89, Q90, Q91, Q92, Q93, Q94, Q95, Q96, Q97, Q98, Q99, Q100, Q101, Q102, Q103, Q104, Q105, Q106, Q107, Q108, Q109, Q110, Q111, Q112, Q113, Q114, Q115, Q116, Q117, Q118, Q119, Q120, Q121, Q122, Q123, Q124, Q125, Q126, Q127, Q128, Q129, Q130, Q131, Q132, Q133, Q134, Q135, Q136, Q137, Q138, Q139, Q140, Q141, Q142, Q143, Q144, Q145, Q146, Q147, Q148, Q149, Q150, Q151, Q152, Q153, Q154, Q155, Q156, Q157, Q158, Q159, Q160, Q161, Q162, Q163, Q164, Q165, Q166, Q167, Q168, Q169, Q170, Q171, Q172, Q173, Q174, Q175, Q176, Q177, Q178, Q179, Q180, Q181, Q182, Q183, Q184, Q185, Q186, Q187, Q188, Q189, Q190, Q191, Q192, Q193, Q194, Q195, Q196, Q197, Q198, Q199, Q200, Q201, Q202, Q203, Q204, Q205, Q206, Q207, Q208, Q209, Q210, Q211, Q212, Q213, Q214, Q215, Q216, Q217, Q218, Q219, Q220, Q221, Q222, Q223, Q224, Q225, Q226, Q227, Q228, Q229, Q230, Q231, Q232, Q233, Q234, Q235, Q236, Q237, Q238, Q239, Q240, Q241, Q242, Q243, Q244, Q245, Q246, Q247, Q248, Q249, Q250, Q251, Q252, Q253, Q254, Q255, Q256, Q257, Q258, Q259, Q260, Q261, Q262, Q263, Q264, Q265, Q266, Q267, Q268, Q269, Q270, Q271, Q272, Q273, Q274, Q275, Q276, Q277, Q278, Q279]), "depth" : 10 * mm, "offsetDistance" : 25 * mm});
        }
        {
            var Q0;
            Q0=qCreatedBy(makeId("Top.planeOp"),FACE);
            var sketch = newSketch(context, id + "F2", { "sketchPlane" : qUnion([Q0])});
            skLineSegment(sketch, "E37.bottom", {"start": v(-13, -13) * mm, "end": v(13, -13) * mm});
            skLineSegment(sketch, "E37.top", {"start": v(-13, 13) * mm, "end": v(13, 13) * mm});
            skLineSegment(sketch, "E37.left", {"start": v(-13, -13) * mm, "end": v(-13, 13) * mm});
            skLineSegment(sketch, "E37.right", {"start": v(13, -13) * mm, "end": v(13, 13) * mm});
            skPoint(sketch, "E37.middle", {"position": v(0, 0) * mm});
            skSolve(sketch);
        }
        {
            var Q0;
            Q0=makeQuery(id+"F2.imprint","IMPRINT",FACE,{"disambiguationData":[TD([[makeQuery(id+"F2.imprint","IMPRINT",EDGE,{"derivedFrom":sQuery(id+"F2.wireOp",EDGE,"E37.bottom")}),1.0]])]});
            extrude(context, id + "F3", {"entities" : qUnion([Q0]), "operationType" : NewBodyOperationType.ADD, "oppositeDirection" : true, "depth" : 2 * mm, "offsetDistance" : 25 * mm});
        }
        {
            var Q0;
            {var subQ0=sQuery(id+"F2.wireOp",EDGE,"E37.top");var subQ1=sQuery(id+"F2.wireOp",EDGE,"E37.left");var subQ2=sQuery(id+"F2.wireOp",EDGE,"E37.bottom");var subQ3=sQuery(id+"F2.wireOp",EDGE,"E37.right");Q0=makeQuery(id+"F3.boolean.opBoolean","SPLIT",FACE,{"disambiguationData":[TD([makeQuery(id+"F1.opExtrude","SWEPT_FACE",FACE,{"disambiguationData":[OSD([sQuery(id+"F0.wireOp",EDGE,"E0.bottom")])]})])],"derivedFrom":makeQuery(id+"F3.opExtrude","CAP_FACE",FACE,{"disambiguationData":[OSD([subQ2,subQ0,subQ1,subQ3])],"isStart":true})});}
            extrude(context, id + "F4", {"entities" : qUnion([Q0]), "operationType" : NewBodyOperationType.ADD, "depth" : 12 * mm, "offsetDistance" : 25 * mm});
        }
        {
            var Q0;
            Q0=makeQuery(id+"F4.opExtrude","CAP_FACE",FACE,{"disambiguationData":[OSD([sQuery(id+"F2.wireOp",EDGE,"E37.bottom"),sQuery(id+"F2.wireOp",EDGE,"E37.top"),sQuery(id+"F2.wireOp",EDGE,"E37.left"),sQuery(id+"F2.wireOp",EDGE,"E37.right")])],"isStart":false});
            var sketch = newSketch(context, id + "F5", { "sketchPlane" : qUnion([Q0])});
            skLineSegment(sketch, "E38", {"start": v(-2.5, 13) * mm, "end": v(-2.5, 9) * mm});
            skLineSegment(sketch, "E39.MirrorCS", {"start": v(2.5, 13) * mm, "end": v(2.5, 9) * mm});
            skLineSegment(sketch, "E40.MirrorCS", {"start": v(2.5, -13) * mm, "end": v(2.5, -9) * mm});
            skLineSegment(sketch, "E41.MirrorCS", {"start": v(-2.5, -13) * mm, "end": v(-2.5, -9) * mm});
            skLineSegment(sketch, "E42", {"start": v(-13, 13) * mm, "end": v(-9, 9) * mm, "construction": true});
            skPoint(sketch, "E43", {"position": v(-10.5, 10.5) * mm});
            skPoint(sketch, "E44.MirrorP", {"position": v(10.5, 10.5) * mm});
            skLineSegment(sketch, "E45.MirrorCS", {"start": v(13, 13) * mm, "end": v(9, 9) * mm, "construction": true});
            skLineSegment(sketch, "E46.MirrorCS", {"start": v(-13, -13) * mm, "end": v(-9, -9) * mm, "construction": true});
            skPoint(sketch, "E47.MirrorP", {"position": v(-10.5, -10.5) * mm});
            skLineSegment(sketch, "E48.MirrorCS", {"start": v(13, -13) * mm, "end": v(9, -9) * mm, "construction": true});
            skPoint(sketch, "E49.MirrorP", {"position": v(10.5, -10.5) * mm});
            skSolve(sketch);
        }
        {
            var Q0;
            {var subQ0=sQuery(id+"F5.wireOp",EDGE,"E38");Q0=makeQuery(id+"F5.imprint","IMPRINT",FACE,{"disambiguationData":[TD([[makeQuery(id+"F5.imprint","IMPRINT",EDGE,{"derivedFrom":subQ0}),1.0]])]});}
            var Q1;
            {var subQ0=sQuery(id+"F5.wireOp",EDGE,"E40.MirrorCS");Q1=makeQuery(id+"F5.imprint","IMPRINT",FACE,{"disambiguationData":[TD([[makeQuery(id+"F5.imprint","IMPRINT",EDGE,{"derivedFrom":subQ0}),1.0]])]});}
            var Q2;
            Q2=makeQuery(id+"F1.opExtrude","CAP_FACE",FACE,{"disambiguationData":[OSD([sQuery(id+"F0.wireOp",EDGE,"E0.bottom"),sQuery(id+"F0.wireOp",EDGE,"E0.top"),sQuery(id+"F0.wireOp",EDGE,"E0.left"),sQuery(id+"F0.wireOp",EDGE,"E0.right"),sQuery(id+"F0.wireOp",EDGE,"E1"),sQuery(id+"F0.wireOp",EDGE,"E2"),sQuery(id+"F0.wireOp",EDGE,"E3"),sQuery(id+"F0.wireOp",EDGE,"E4"),sQuery(id+"F0.wireOp",EDGE,"E5"),sQuery(id+"F0.wireOp",EDGE,"E6"),sQuery(id+"F0.wireOp",EDGE,"E7"),sQuery(id+"F0.wireOp",EDGE,"E8"),sQuery(id+"F0.wireOp",EDGE,"E9"),sQuery(id+"F0.wireOp",EDGE,"E10"),sQuery(id+"F0.wireOp",EDGE,"E11"),sQuery(id+"F0.wireOp",EDGE,"E12"),sQuery(id+"F0.wireOp",EDGE,"E13"),sQuery(id+"F0.wireOp",EDGE,"E14"),sQuery(id+"F0.wireOp",EDGE,"E15"),sQuery(id+"F0.wireOp",EDGE,"E16"),sQuery(id+"F0.wireOp",EDGE,"E17"),sQuery(id+"F0.wireOp",EDGE,"E18"),sQuery(id+"F0.wireOp",EDGE,"E19"),sQuery(id+"F0.wireOp",EDGE,"E20"),sQuery(id+"F0.wireOp",EDGE,"E21"),sQuery(id+"F0.wireOp",EDGE,"E22"),sQuery(id+"F0.wireOp",EDGE,"E23"),sQuery(id+"F0.wireOp",EDGE,"E24"),sQuery(id+"F0.wireOp",EDGE,"E25"),sQuery(id+"F0.wireOp",EDGE,"E26"),sQuery(id+"F0.wireOp",EDGE,"E27"),sQuery(id+"F0.wireOp",EDGE,"E28"),sQuery(id+"F0.wireOp",EDGE,"E29"),sQuery(id+"F0.wireOp",EDGE,"E30"),sQuery(id+"F0.wireOp",EDGE,"E31"),sQuery(id+"F0.wireOp",EDGE,"E32"),sQuery(id+"F0.wireOp",EDGE,"E33"),sQuery(id+"F0.wireOp",EDGE,"E34"),sQuery(id+"F0.wireOp",EDGE,"E35"),sQuery(id+"F0.wireOp",EDGE,"E36")])],"isStart":false});
            extrude(context, id + "F6", {"entities" : qUnion([Q0, Q1]), "operationType" : NewBodyOperationType.REMOVE, "endBound" : BoundingType.UP_TO_SURFACE, "oppositeDirection" : true, "depth" : 25 * mm, "endBoundEntityFace" : qUnion([Q2]), "offsetDistance" : 25 * mm});
        }
        {
            var Q0;
            Q0=sQuery(id+"F5.wireOp",VERTEX,"E43");
            var Q1;
            Q1=sQuery(id+"F5.wireOp",VERTEX,"E44.MirrorP");
            var Q2;
            Q2=sQuery(id+"F5.wireOp",VERTEX,"E49.MirrorP");
            var Q3;
            Q3=sQuery(id+"F5.wireOp",VERTEX,"E47.MirrorP");
            var Q4;
            Q4=makeQuery(id+"F1.opExtrude","SWEPT_BODY",BODY,{"disambiguationData":[OSD([sQuery(id+"F0.wireOp",EDGE,"E0.bottom"),sQuery(id+"F0.wireOp",EDGE,"E0.top"),sQuery(id+"F0.wireOp",EDGE,"E0.left"),sQuery(id+"F0.wireOp",EDGE,"E0.right"),sQuery(id+"F0.wireOp",EDGE,"E1"),sQuery(id+"F0.wireOp",EDGE,"E2"),sQuery(id+"F0.wireOp",EDGE,"E3"),sQuery(id+"F0.wireOp",EDGE,"E4"),sQuery(id+"F0.wireOp",EDGE,"E5"),sQuery(id+"F0.wireOp",EDGE,"E6"),sQuery(id+"F0.wireOp",EDGE,"E7"),sQuery(id+"F0.wireOp",EDGE,"E8"),sQuery(id+"F0.wireOp",EDGE,"E9"),sQuery(id+"F0.wireOp",EDGE,"E10"),sQuery(id+"F0.wireOp",EDGE,"E11"),sQuery(id+"F0.wireOp",EDGE,"E12"),sQuery(id+"F0.wireOp",EDGE,"E13"),sQuery(id+"F0.wireOp",EDGE,"E14"),sQuery(id+"F0.wireOp",EDGE,"E15"),sQuery(id+"F0.wireOp",EDGE,"E16"),sQuery(id+"F0.wireOp",EDGE,"E17"),sQuery(id+"F0.wireOp",EDGE,"E18"),sQuery(id+"F0.wireOp",EDGE,"E19"),sQuery(id+"F0.wireOp",EDGE,"E20"),sQuery(id+"F0.wireOp",EDGE,"E21"),sQuery(id+"F0.wireOp",EDGE,"E22"),sQuery(id+"F0.wireOp",EDGE,"E23"),sQuery(id+"F0.wireOp",EDGE,"E24"),sQuery(id+"F0.wireOp",EDGE,"E25"),sQuery(id+"F0.wireOp",EDGE,"E26"),sQuery(id+"F0.wireOp",EDGE,"E27"),sQuery(id+"F0.wireOp",EDGE,"E28"),sQuery(id+"F0.wireOp",EDGE,"E29"),sQuery(id+"F0.wireOp",EDGE,"E30"),sQuery(id+"F0.wireOp",EDGE,"E31"),sQuery(id+"F0.wireOp",EDGE,"E32"),sQuery(id+"F0.wireOp",EDGE,"E33"),sQuery(id+"F0.wireOp",EDGE,"E34"),sQuery(id+"F0.wireOp",EDGE,"E35"),sQuery(id+"F0.wireOp",EDGE,"E36")])]});
            hole(context, id + "F7", {"style" : HoleStyle.SIMPLE, "endStyle" : HoleEndStyle.BLIND, "standardTappedOrClearance" : lookupTablePath({ "standard" : "ISO", "engagement" : "50%", "pitch" : "0.5 mm", "size" : "M3", "type" : "Tapped" }), "standardBlindInLast" : lookupTablePath({ "standard" : "ISO", "fit" : "Normal", "engagement" : "50%", "pitch" : "0.5 mm", "size" : "M3", "type" : "Clearance & tapped" }), "holeDiameter" : 2.7 * mm, "majorDiameter" : 3 * mm, "showTappedDepth" : true, "holeDepth" : 3.5 * mm, "isTappedThrough" : true, "tappedDepth" : 2 * mm, "tapClearance" : 3, "locations" : qUnion([Q0, Q1, Q2, Q3]), "scope" : qUnion([Q4])});
        }
    });
